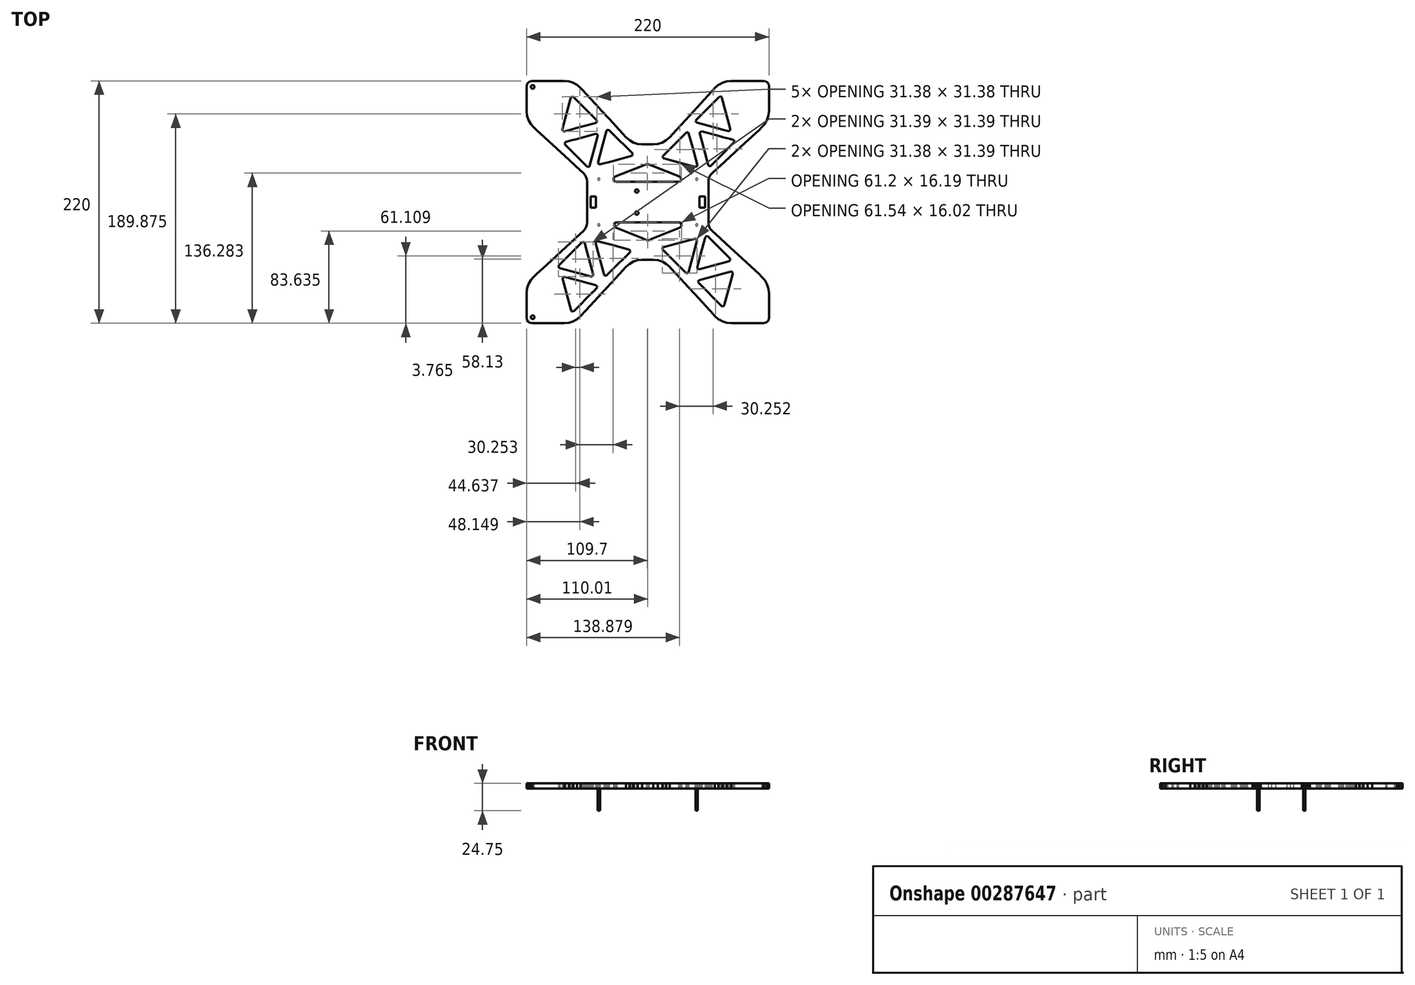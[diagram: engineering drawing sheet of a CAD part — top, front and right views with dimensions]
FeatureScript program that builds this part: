
annotation { "Feature Type Name" : "Feature", "Feature Type Description" : "" }
export const myFeature = defineFeature(function(context is Context, id is Id, definition is map)
    precondition{}
    {
        {
            var Q0;
            Q0=qCreatedBy(makeId("Top.planeOp"),FACE);
            var sketch = newSketch(context, id + "F0", { "sketchPlane" : qUnion([Q0])});
            skLineSegment(sketch, "E0", {"start": v(110, -105) * mm, "end": v(109.97, -105.11) * mm});
            skLineSegment(sketch, "E1", {"start": v(109.97, -105.11) * mm, "end": v(109.33, -107.5) * mm});
            skLineSegment(sketch, "E2", {"start": v(109.33, -107.5) * mm, "end": v(107.5, -109.33) * mm});
            skLineSegment(sketch, "E3", {"start": v(107.5, -109.33) * mm, "end": v(105.11, -109.97) * mm});
            skLineSegment(sketch, "E4", {"start": v(105.11, -109.97) * mm, "end": v(105, -110) * mm});
            skLineSegment(sketch, "E5", {"start": v(105, -110) * mm, "end": v(75.71, -110) * mm});
            skLineSegment(sketch, "E6", {"start": v(75.71, -110) * mm, "end": v(71.6, -109.58) * mm});
            skLineSegment(sketch, "E7", {"start": v(71.6, -109.58) * mm, "end": v(67.68, -108.32) * mm});
            skLineSegment(sketch, "E8", {"start": v(67.68, -108.32) * mm, "end": v(65.54, -107.1) * mm});
            skLineSegment(sketch, "E9", {"start": v(65.54, -107.1) * mm, "end": v(64.1, -106.29) * mm});
            skLineSegment(sketch, "E10", {"start": v(64.1, -106.29) * mm, "end": v(61, -103.56) * mm});
            skLineSegment(sketch, "E11", {"start": v(61, -103.56) * mm, "end": v(60.02, -102.49) * mm});
            skLineSegment(sketch, "E12", {"start": v(60.02, -102.49) * mm, "end": v(59.43, -101.85) * mm});
            skLineSegment(sketch, "E13", {"start": v(59.43, -101.85) * mm, "end": v(42.66, -83.66) * mm});
            skLineSegment(sketch, "E14", {"start": v(42.66, -83.66) * mm, "end": v(37.1, -77.62) * mm});
            skLineSegment(sketch, "E15", {"start": v(37.1, -77.62) * mm, "end": v(25.96, -65.54) * mm});
            skLineSegment(sketch, "E16", {"start": v(25.96, -65.54) * mm, "end": v(20.43, -59.54) * mm});
            skLineSegment(sketch, "E17", {"start": v(20.43, -59.54) * mm, "end": v(19.77, -58.82) * mm});
            skLineSegment(sketch, "E18", {"start": v(19.77, -58.82) * mm, "end": v(16.67, -56.1) * mm});
            skLineSegment(sketch, "E19", {"start": v(16.67, -56.1) * mm, "end": v(13.09, -54.06) * mm});
            skLineSegment(sketch, "E20", {"start": v(13.09, -54.06) * mm, "end": v(9.16, -52.8) * mm});
            skLineSegment(sketch, "E21", {"start": v(9.16, -52.8) * mm, "end": v(5.06, -52.37) * mm});
            skLineSegment(sketch, "E22", {"start": v(5.06, -52.37) * mm, "end": v(-5.06, -52.37) * mm});
            skLineSegment(sketch, "E23", {"start": v(-5.06, -52.37) * mm, "end": v(-9.16, -52.8) * mm});
            skLineSegment(sketch, "E24", {"start": v(-9.16, -52.8) * mm, "end": v(-13.1, -54.06) * mm});
            skLineSegment(sketch, "E25", {"start": v(-13.1, -54.06) * mm, "end": v(-16.67, -56.1) * mm});
            skLineSegment(sketch, "E26", {"start": v(-16.67, -56.1) * mm, "end": v(-19.77, -58.82) * mm});
            skLineSegment(sketch, "E27", {"start": v(-19.77, -58.82) * mm, "end": v(-25.96, -65.54) * mm});
            skLineSegment(sketch, "E28", {"start": v(-25.96, -65.54) * mm, "end": v(-32.77, -72.92) * mm});
            skLineSegment(sketch, "E29", {"start": v(-32.77, -72.92) * mm, "end": v(-37.77, -78.35) * mm});
            skLineSegment(sketch, "E30", {"start": v(-37.77, -78.35) * mm, "end": v(-38.62, -79.27) * mm});
            skLineSegment(sketch, "E31", {"start": v(-38.62, -79.27) * mm, "end": v(-39.42, -80.14) * mm});
            skLineSegment(sketch, "E32", {"start": v(-39.42, -80.14) * mm, "end": v(-41.06, -81.92) * mm});
            skLineSegment(sketch, "E33", {"start": v(-41.06, -81.92) * mm, "end": v(-56.16, -98.3) * mm});
            skLineSegment(sketch, "E34", {"start": v(-56.16, -98.3) * mm, "end": v(-61, -103.56) * mm});
            skLineSegment(sketch, "E35", {"start": v(-61, -103.56) * mm, "end": v(-64.1, -106.29) * mm});
            skLineSegment(sketch, "E36", {"start": v(-64.1, -106.29) * mm, "end": v(-65.54, -107.1) * mm});
            skLineSegment(sketch, "E37", {"start": v(-65.54, -107.1) * mm, "end": v(-67.68, -108.32) * mm});
            skLineSegment(sketch, "E38", {"start": v(-67.68, -108.32) * mm, "end": v(-71.6, -109.58) * mm});
            skLineSegment(sketch, "E39", {"start": v(-71.6, -109.58) * mm, "end": v(-75.71, -110) * mm});
            skLineSegment(sketch, "E40", {"start": v(-75.71, -110) * mm, "end": v(-105, -110) * mm});
            skLineSegment(sketch, "E41", {"start": v(-105, -110) * mm, "end": v(-106.91, -109.62) * mm});
            skLineSegment(sketch, "E42", {"start": v(-106.91, -109.62) * mm, "end": v(-108.53, -108.54) * mm});
            skLineSegment(sketch, "E43", {"start": v(-108.53, -108.54) * mm, "end": v(-109.62, -106.92) * mm});
            skLineSegment(sketch, "E44", {"start": v(-109.62, -106.92) * mm, "end": v(-110, -105) * mm});
            skLineSegment(sketch, "E45", {"start": v(-110, -105) * mm, "end": v(-110, -82.51) * mm});
            skLineSegment(sketch, "E46", {"start": v(-110, -82.51) * mm, "end": v(-109.58, -78.41) * mm});
            skLineSegment(sketch, "E47", {"start": v(-109.58, -78.41) * mm, "end": v(-108.32, -74.48) * mm});
            skLineSegment(sketch, "E48", {"start": v(-108.32, -74.48) * mm, "end": v(-106.28, -70.9) * mm});
            skLineSegment(sketch, "E49", {"start": v(-106.28, -70.9) * mm, "end": v(-103.55, -67.8) * mm});
            skLineSegment(sketch, "E50", {"start": v(-103.55, -67.8) * mm, "end": v(-101.1, -65.54) * mm});
            skLineSegment(sketch, "E51", {"start": v(-101.1, -65.54) * mm, "end": v(-91.63, -56.8) * mm});
            skLineSegment(sketch, "E52", {"start": v(-91.63, -56.8) * mm, "end": v(-65.54, -32.76) * mm});
            skLineSegment(sketch, "E53", {"start": v(-65.54, -32.76) * mm, "end": v(-58.22, -26.01) * mm});
            skLineSegment(sketch, "E54", {"start": v(-58.22, -26.01) * mm, "end": v(-56.86, -24.47) * mm});
            skLineSegment(sketch, "E55", {"start": v(-56.86, -24.47) * mm, "end": v(-55.84, -22.68) * mm});
            skLineSegment(sketch, "E56", {"start": v(-55.84, -22.68) * mm, "end": v(-55.21, -20.71) * mm});
            skLineSegment(sketch, "E57", {"start": v(-55.21, -20.71) * mm, "end": v(-55, -18.66) * mm});
            skLineSegment(sketch, "E58", {"start": v(-55, -18.66) * mm, "end": v(-55, 18.67) * mm});
            skLineSegment(sketch, "E59", {"start": v(-55, 18.67) * mm, "end": v(-55.21, 20.72) * mm});
            skLineSegment(sketch, "E60", {"start": v(-55.21, 20.72) * mm, "end": v(-55.84, 22.68) * mm});
            skLineSegment(sketch, "E61", {"start": v(-55.84, 22.68) * mm, "end": v(-56.86, 24.47) * mm});
            skLineSegment(sketch, "E62", {"start": v(-56.86, 24.47) * mm, "end": v(-58.22, 26.02) * mm});
            skLineSegment(sketch, "E63", {"start": v(-58.22, 26.02) * mm, "end": v(-65.54, 32.76) * mm});
            skLineSegment(sketch, "E64", {"start": v(-65.54, 32.76) * mm, "end": v(-66.26, 33.43) * mm});
            skLineSegment(sketch, "E65", {"start": v(-66.26, 33.43) * mm, "end": v(-75.44, 41.9) * mm});
            skLineSegment(sketch, "E66", {"start": v(-75.44, 41.9) * mm, "end": v(-101.1, 65.54) * mm});
            skLineSegment(sketch, "E67", {"start": v(-101.1, 65.54) * mm, "end": v(-103.55, 67.8) * mm});
            skLineSegment(sketch, "E68", {"start": v(-103.55, 67.8) * mm, "end": v(-106.28, 70.9) * mm});
            skLineSegment(sketch, "E69", {"start": v(-106.28, 70.9) * mm, "end": v(-108.32, 74.48) * mm});
            skLineSegment(sketch, "E70", {"start": v(-108.32, 74.48) * mm, "end": v(-109.58, 78.41) * mm});
            skLineSegment(sketch, "E71", {"start": v(-109.58, 78.41) * mm, "end": v(-110, 82.51) * mm});
            skLineSegment(sketch, "E72", {"start": v(-110, 82.51) * mm, "end": v(-110, 105) * mm});
            skLineSegment(sketch, "E73", {"start": v(-110, 105) * mm, "end": v(-109.97, 105.12) * mm});
            skLineSegment(sketch, "E74", {"start": v(-109.97, 105.12) * mm, "end": v(-109.33, 107.5) * mm});
            skLineSegment(sketch, "E75", {"start": v(-109.33, 107.5) * mm, "end": v(-108.87, 107.96) * mm});
            skLineSegment(sketch, "E76", {"start": v(-108.87, 107.96) * mm, "end": v(-107.5, 109.33) * mm});
            skLineSegment(sketch, "E77", {"start": v(-107.5, 109.33) * mm, "end": v(-105.11, 109.97) * mm});
            skLineSegment(sketch, "E78", {"start": v(-105.11, 109.97) * mm, "end": v(-105, 110) * mm});
            skLineSegment(sketch, "E79", {"start": v(-105, 110) * mm, "end": v(-75.71, 110) * mm});
            skLineSegment(sketch, "E80", {"start": v(-75.71, 110) * mm, "end": v(-71.6, 109.58) * mm});
            skLineSegment(sketch, "E81", {"start": v(-71.6, 109.58) * mm, "end": v(-67.68, 108.32) * mm});
            skLineSegment(sketch, "E82", {"start": v(-67.68, 108.32) * mm, "end": v(-65.54, 107.1) * mm});
            skLineSegment(sketch, "E83", {"start": v(-65.54, 107.1) * mm, "end": v(-64.1, 106.29) * mm});
            skLineSegment(sketch, "E84", {"start": v(-64.1, 106.29) * mm, "end": v(-61, 103.56) * mm});
            skLineSegment(sketch, "E85", {"start": v(-61, 103.56) * mm, "end": v(-59.4, 101.81) * mm});
            skLineSegment(sketch, "E86", {"start": v(-59.4, 101.81) * mm, "end": v(-43.95, 85.06) * mm});
            skLineSegment(sketch, "E87", {"start": v(-43.95, 85.06) * mm, "end": v(-42.3, 83.27) * mm});
            skLineSegment(sketch, "E88", {"start": v(-42.3, 83.27) * mm, "end": v(-34.8, 75.14) * mm});
            skLineSegment(sketch, "E89", {"start": v(-34.8, 75.14) * mm, "end": v(-25.96, 65.54) * mm});
            skLineSegment(sketch, "E90", {"start": v(-25.96, 65.54) * mm, "end": v(-19.77, 58.82) * mm});
            skLineSegment(sketch, "E91", {"start": v(-19.77, 58.82) * mm, "end": v(-16.67, 56.1) * mm});
            skLineSegment(sketch, "E92", {"start": v(-16.67, 56.1) * mm, "end": v(-13.1, 54.06) * mm});
            skLineSegment(sketch, "E93", {"start": v(-13.1, 54.06) * mm, "end": v(-9.16, 52.8) * mm});
            skLineSegment(sketch, "E94", {"start": v(-9.16, 52.8) * mm, "end": v(-5.06, 52.38) * mm});
            skLineSegment(sketch, "E95", {"start": v(-5.06, 52.38) * mm, "end": v(5.06, 52.38) * mm});
            skLineSegment(sketch, "E96", {"start": v(5.06, 52.38) * mm, "end": v(9.16, 52.8) * mm});
            skLineSegment(sketch, "E97", {"start": v(9.16, 52.8) * mm, "end": v(13.09, 54.06) * mm});
            skLineSegment(sketch, "E98", {"start": v(13.09, 54.06) * mm, "end": v(16.67, 56.1) * mm});
            skLineSegment(sketch, "E99", {"start": v(16.67, 56.1) * mm, "end": v(19.77, 58.82) * mm});
            skLineSegment(sketch, "E100", {"start": v(19.77, 58.82) * mm, "end": v(25.96, 65.54) * mm});
            skLineSegment(sketch, "E101", {"start": v(25.96, 65.54) * mm, "end": v(34.46, 74.76) * mm});
            skLineSegment(sketch, "E102", {"start": v(34.46, 74.76) * mm, "end": v(45, 86.2) * mm});
            skLineSegment(sketch, "E103", {"start": v(45, 86.2) * mm, "end": v(61, 103.56) * mm});
            skLineSegment(sketch, "E104", {"start": v(61, 103.56) * mm, "end": v(64.1, 106.29) * mm});
            skLineSegment(sketch, "E105", {"start": v(64.1, 106.29) * mm, "end": v(65.54, 107.1) * mm});
            skLineSegment(sketch, "E106", {"start": v(65.54, 107.1) * mm, "end": v(67.68, 108.32) * mm});
            skLineSegment(sketch, "E107", {"start": v(67.68, 108.32) * mm, "end": v(71.6, 109.58) * mm});
            skLineSegment(sketch, "E108", {"start": v(71.6, 109.58) * mm, "end": v(75.71, 110) * mm});
            skLineSegment(sketch, "E109", {"start": v(75.71, 110) * mm, "end": v(105, 110) * mm});
            skLineSegment(sketch, "E110", {"start": v(105, 110) * mm, "end": v(106.91, 109.62) * mm});
            skLineSegment(sketch, "E111", {"start": v(106.91, 109.62) * mm, "end": v(107.98, 108.9) * mm});
            skLineSegment(sketch, "E112", {"start": v(107.98, 108.9) * mm, "end": v(108.53, 108.54) * mm});
            skLineSegment(sketch, "E113", {"start": v(108.53, 108.54) * mm, "end": v(109.62, 106.92) * mm});
            skLineSegment(sketch, "E114", {"start": v(109.62, 106.92) * mm, "end": v(109.98, 105.13) * mm});
            skLineSegment(sketch, "E115", {"start": v(109.98, 105.13) * mm, "end": v(110, 105) * mm});
            skLineSegment(sketch, "E116", {"start": v(110, 105) * mm, "end": v(110, 82.51) * mm});
            skLineSegment(sketch, "E117", {"start": v(110, 82.51) * mm, "end": v(109.58, 78.41) * mm});
            skLineSegment(sketch, "E118", {"start": v(109.58, 78.41) * mm, "end": v(108.32, 74.48) * mm});
            skLineSegment(sketch, "E119", {"start": v(108.32, 74.48) * mm, "end": v(106.28, 70.9) * mm});
            skLineSegment(sketch, "E120", {"start": v(106.28, 70.9) * mm, "end": v(103.56, 67.8) * mm});
            skLineSegment(sketch, "E121", {"start": v(103.56, 67.8) * mm, "end": v(101.1, 65.54) * mm});
            skLineSegment(sketch, "E122", {"start": v(101.1, 65.54) * mm, "end": v(88.12, 53.58) * mm});
            skLineSegment(sketch, "E123", {"start": v(88.12, 53.58) * mm, "end": v(65.54, 32.76) * mm});
            skLineSegment(sketch, "E124", {"start": v(65.54, 32.76) * mm, "end": v(63.4, 30.8) * mm});
            skLineSegment(sketch, "E125", {"start": v(63.4, 30.8) * mm, "end": v(58.22, 26.02) * mm});
            skLineSegment(sketch, "E126", {"start": v(58.22, 26.02) * mm, "end": v(56.86, 24.47) * mm});
            skLineSegment(sketch, "E127", {"start": v(56.86, 24.47) * mm, "end": v(55.84, 22.68) * mm});
            skLineSegment(sketch, "E128", {"start": v(55.84, 22.68) * mm, "end": v(55.21, 20.72) * mm});
            skLineSegment(sketch, "E129", {"start": v(55.21, 20.72) * mm, "end": v(55, 18.67) * mm});
            skLineSegment(sketch, "E130", {"start": v(55, 18.67) * mm, "end": v(55, -18.66) * mm});
            skLineSegment(sketch, "E131", {"start": v(55, -18.66) * mm, "end": v(55.21, -20.71) * mm});
            skLineSegment(sketch, "E132", {"start": v(55.21, -20.71) * mm, "end": v(55.84, -22.68) * mm});
            skLineSegment(sketch, "E133", {"start": v(55.84, -22.68) * mm, "end": v(56.86, -24.47) * mm});
            skLineSegment(sketch, "E134", {"start": v(56.86, -24.47) * mm, "end": v(58.22, -26.01) * mm});
            skLineSegment(sketch, "E135", {"start": v(58.22, -26.01) * mm, "end": v(65.54, -32.76) * mm});
            skLineSegment(sketch, "E136", {"start": v(65.54, -32.76) * mm, "end": v(66.29, -33.45) * mm});
            skLineSegment(sketch, "E137", {"start": v(66.29, -33.45) * mm, "end": v(75, -41.48) * mm});
            skLineSegment(sketch, "E138", {"start": v(75, -41.48) * mm, "end": v(81.72, -47.68) * mm});
            skLineSegment(sketch, "E139", {"start": v(81.72, -47.68) * mm, "end": v(101.1, -65.54) * mm});
            skLineSegment(sketch, "E140", {"start": v(101.1, -65.54) * mm, "end": v(103.56, -67.8) * mm});
            skLineSegment(sketch, "E141", {"start": v(103.56, -67.8) * mm, "end": v(106.28, -70.9) * mm});
            skLineSegment(sketch, "E142", {"start": v(106.28, -70.9) * mm, "end": v(108.32, -74.48) * mm});
            skLineSegment(sketch, "E143", {"start": v(108.32, -74.48) * mm, "end": v(109.58, -78.41) * mm});
            skLineSegment(sketch, "E144", {"start": v(109.58, -78.41) * mm, "end": v(110, -82.51) * mm});
            skLineSegment(sketch, "E145", {"start": v(110, -82.51) * mm, "end": v(110, -105) * mm});
            skLineSegment(sketch, "E146", {"start": v(-43.2, 34.18) * mm, "end": v(-32.77, 36.98) * mm});
            skLineSegment(sketch, "E147", {"start": v(-32.77, 36.98) * mm, "end": v(-14.76, 41.8) * mm});
            skLineSegment(sketch, "E148", {"start": v(-14.76, 41.8) * mm, "end": v(-13.92, 42.4) * mm});
            skLineSegment(sketch, "E149", {"start": v(-13.92, 42.4) * mm, "end": v(-13.66, 43.38) * mm});
            skLineSegment(sketch, "E150", {"start": v(-13.66, 43.38) * mm, "end": v(-14.1, 44.31) * mm});
            skLineSegment(sketch, "E151", {"start": v(-14.1, 44.31) * mm, "end": v(-32.77, 62.99) * mm});
            skLineSegment(sketch, "E152", {"start": v(-32.77, 62.99) * mm, "end": v(-34.9, 65.12) * mm});
            skLineSegment(sketch, "E153", {"start": v(-34.9, 65.12) * mm, "end": v(-34.91, 65.13) * mm});
            skLineSegment(sketch, "E154", {"start": v(-34.91, 65.13) * mm, "end": v(-35.78, 65.54) * mm});
            skLineSegment(sketch, "E155", {"start": v(-35.78, 65.54) * mm, "end": v(-35.84, 65.57) * mm});
            skLineSegment(sketch, "E156", {"start": v(-35.84, 65.57) * mm, "end": v(-35.95, 65.54) * mm});
            skLineSegment(sketch, "E157", {"start": v(-35.95, 65.54) * mm, "end": v(-36.83, 65.3) * mm});
            skLineSegment(sketch, "E158", {"start": v(-36.83, 65.3) * mm, "end": v(-37.42, 64.46) * mm});
            skLineSegment(sketch, "E159", {"start": v(-37.42, 64.46) * mm, "end": v(-37.43, 64.44) * mm});
            skLineSegment(sketch, "E160", {"start": v(-37.43, 64.44) * mm, "end": v(-41.52, 49.15) * mm});
            skLineSegment(sketch, "E161", {"start": v(-41.52, 49.15) * mm, "end": v(-45.04, 36.02) * mm});
            skLineSegment(sketch, "E162", {"start": v(-45.04, 36.02) * mm, "end": v(-44.95, 35) * mm});
            skLineSegment(sketch, "E163", {"start": v(-44.95, 35) * mm, "end": v(-44.23, 34.27) * mm});
            skLineSegment(sketch, "E164", {"start": v(-44.23, 34.27) * mm, "end": v(-43.2, 34.18) * mm});
            skLineSegment(sketch, "E165", {"start": v(-58.87, -36.18) * mm, "end": v(-59.8, -36.61) * mm});
            skLineSegment(sketch, "E166", {"start": v(-59.8, -36.61) * mm, "end": v(-65.54, -42.35) * mm});
            skLineSegment(sketch, "E167", {"start": v(-65.54, -42.35) * mm, "end": v(-80.62, -57.43) * mm});
            skLineSegment(sketch, "E168", {"start": v(-80.62, -57.43) * mm, "end": v(-81.06, -58.36) * mm});
            skLineSegment(sketch, "E169", {"start": v(-81.06, -58.36) * mm, "end": v(-80.79, -59.35) * mm});
            skLineSegment(sketch, "E170", {"start": v(-80.79, -59.35) * mm, "end": v(-79.95, -59.94) * mm});
            skLineSegment(sketch, "E171", {"start": v(-79.95, -59.94) * mm, "end": v(-65.54, -63.8) * mm});
            skLineSegment(sketch, "E172", {"start": v(-65.54, -63.8) * mm, "end": v(-59.07, -65.54) * mm});
            skLineSegment(sketch, "E173", {"start": v(-59.07, -65.54) * mm, "end": v(-51.5, -67.56) * mm});
            skLineSegment(sketch, "E174", {"start": v(-51.5, -67.56) * mm, "end": v(-50.49, -67.47) * mm});
            skLineSegment(sketch, "E175", {"start": v(-50.49, -67.47) * mm, "end": v(-49.76, -66.75) * mm});
            skLineSegment(sketch, "E176", {"start": v(-49.76, -66.75) * mm, "end": v(-49.67, -65.73) * mm});
            skLineSegment(sketch, "E177", {"start": v(-49.67, -65.73) * mm, "end": v(-49.72, -65.54) * mm});
            skLineSegment(sketch, "E178", {"start": v(-49.72, -65.54) * mm, "end": v(-49.74, -65.46) * mm});
            skLineSegment(sketch, "E179", {"start": v(-49.74, -65.46) * mm, "end": v(-55.38, -44.43) * mm});
            skLineSegment(sketch, "E180", {"start": v(-55.38, -44.43) * mm, "end": v(-57.3, -37.28) * mm});
            skLineSegment(sketch, "E181", {"start": v(-57.3, -37.28) * mm, "end": v(-57.81, -36.53) * mm});
            skLineSegment(sketch, "E182", {"start": v(-57.81, -36.53) * mm, "end": v(-57.88, -36.44) * mm});
            skLineSegment(sketch, "E183", {"start": v(-57.88, -36.44) * mm, "end": v(-58.87, -36.18) * mm});
            skLineSegment(sketch, "E184", {"start": v(65.54, 66.43) * mm, "end": v(68.87, 65.54) * mm});
            skLineSegment(sketch, "E185", {"start": v(68.87, 65.54) * mm, "end": v(72.99, 64.43) * mm});
            skLineSegment(sketch, "E186", {"start": v(72.99, 64.43) * mm, "end": v(74, 64.52) * mm});
            skLineSegment(sketch, "E187", {"start": v(74, 64.52) * mm, "end": v(74.73, 65.25) * mm});
            skLineSegment(sketch, "E188", {"start": v(74.73, 65.25) * mm, "end": v(74.76, 65.54) * mm});
            skLineSegment(sketch, "E189", {"start": v(74.76, 65.54) * mm, "end": v(74.82, 66.27) * mm});
            skLineSegment(sketch, "E190", {"start": v(74.82, 66.27) * mm, "end": v(67.2, 94.71) * mm});
            skLineSegment(sketch, "E191", {"start": v(67.2, 94.71) * mm, "end": v(66.62, 95.55) * mm});
            skLineSegment(sketch, "E192", {"start": v(66.62, 95.55) * mm, "end": v(65.62, 95.82) * mm});
            skLineSegment(sketch, "E193", {"start": v(65.62, 95.82) * mm, "end": v(65.54, 95.78) * mm});
            skLineSegment(sketch, "E194", {"start": v(65.54, 95.78) * mm, "end": v(64.7, 95.39) * mm});
            skLineSegment(sketch, "E195", {"start": v(64.7, 95.39) * mm, "end": v(43.87, 74.57) * mm});
            skLineSegment(sketch, "E196", {"start": v(43.87, 74.57) * mm, "end": v(43.44, 73.64) * mm});
            skLineSegment(sketch, "E197", {"start": v(43.44, 73.64) * mm, "end": v(43.7, 72.65) * mm});
            skLineSegment(sketch, "E198", {"start": v(43.7, 72.65) * mm, "end": v(44.55, 72.06) * mm});
            skLineSegment(sketch, "E199", {"start": v(44.55, 72.06) * mm, "end": v(65.54, 66.43) * mm});
            skLineSegment(sketch, "E200", {"start": v(-17.01, -43.07) * mm, "end": v(-32.77, -38.85) * mm});
            skLineSegment(sketch, "E201", {"start": v(-32.77, -38.85) * mm, "end": v(-45.45, -35.45) * mm});
            skLineSegment(sketch, "E202", {"start": v(-45.45, -35.45) * mm, "end": v(-46.48, -35.54) * mm});
            skLineSegment(sketch, "E203", {"start": v(-46.48, -35.54) * mm, "end": v(-47.2, -36.26) * mm});
            skLineSegment(sketch, "E204", {"start": v(-47.2, -36.26) * mm, "end": v(-47.3, -37.28) * mm});
            skLineSegment(sketch, "E205", {"start": v(-47.3, -37.28) * mm, "end": v(-39.72, -65.54) * mm});
            skLineSegment(sketch, "E206", {"start": v(-39.72, -65.54) * mm, "end": v(-39.67, -65.73) * mm});
            skLineSegment(sketch, "E207", {"start": v(-39.67, -65.73) * mm, "end": v(-39.08, -66.57) * mm});
            skLineSegment(sketch, "E208", {"start": v(-39.08, -66.57) * mm, "end": v(-38.1, -66.83) * mm});
            skLineSegment(sketch, "E209", {"start": v(-38.1, -66.83) * mm, "end": v(-37.16, -66.4) * mm});
            skLineSegment(sketch, "E210", {"start": v(-37.16, -66.4) * mm, "end": v(-36.3, -65.54) * mm});
            skLineSegment(sketch, "E211", {"start": v(-36.3, -65.54) * mm, "end": v(-32.77, -62) * mm});
            skLineSegment(sketch, "E212", {"start": v(-32.77, -62) * mm, "end": v(-16.34, -45.58) * mm});
            skLineSegment(sketch, "E213", {"start": v(-16.34, -45.58) * mm, "end": v(-15.9, -44.65) * mm});
            skLineSegment(sketch, "E214", {"start": v(-15.9, -44.65) * mm, "end": v(-16.17, -43.65) * mm});
            skLineSegment(sketch, "E215", {"start": v(-16.17, -43.65) * mm, "end": v(-17.01, -43.07) * mm});
            skLineSegment(sketch, "E216", {"start": v(78.32, 55.84) * mm, "end": v(77.48, 56.43) * mm});
            skLineSegment(sketch, "E217", {"start": v(77.48, 56.43) * mm, "end": v(74.05, 57.35) * mm});
            skLineSegment(sketch, "E218", {"start": v(74.05, 57.35) * mm, "end": v(68.35, 58.88) * mm});
            skLineSegment(sketch, "E219", {"start": v(68.35, 58.88) * mm, "end": v(65.54, 59.63) * mm});
            skLineSegment(sketch, "E220", {"start": v(65.54, 59.63) * mm, "end": v(49.04, 64.05) * mm});
            skLineSegment(sketch, "E221", {"start": v(49.04, 64.05) * mm, "end": v(48.02, 63.96) * mm});
            skLineSegment(sketch, "E222", {"start": v(48.02, 63.96) * mm, "end": v(47.3, 63.24) * mm});
            skLineSegment(sketch, "E223", {"start": v(47.3, 63.24) * mm, "end": v(47.2, 62.21) * mm});
            skLineSegment(sketch, "E224", {"start": v(47.2, 62.21) * mm, "end": v(50.7, 49.15) * mm});
            skLineSegment(sketch, "E225", {"start": v(50.7, 49.15) * mm, "end": v(54.82, 33.77) * mm});
            skLineSegment(sketch, "E226", {"start": v(54.82, 33.77) * mm, "end": v(55.41, 32.93) * mm});
            skLineSegment(sketch, "E227", {"start": v(55.41, 32.93) * mm, "end": v(56.02, 32.77) * mm});
            skLineSegment(sketch, "E228", {"start": v(56.02, 32.77) * mm, "end": v(56.4, 32.66) * mm});
            skLineSegment(sketch, "E229", {"start": v(56.4, 32.66) * mm, "end": v(56.62, 32.77) * mm});
            skLineSegment(sketch, "E230", {"start": v(56.62, 32.77) * mm, "end": v(57.33, 33.1) * mm});
            skLineSegment(sketch, "E231", {"start": v(57.33, 33.1) * mm, "end": v(65.54, 41.3) * mm});
            skLineSegment(sketch, "E232", {"start": v(65.54, 41.3) * mm, "end": v(78.16, 53.92) * mm});
            skLineSegment(sketch, "E233", {"start": v(78.16, 53.92) * mm, "end": v(78.59, 54.85) * mm});
            skLineSegment(sketch, "E234", {"start": v(78.59, 54.85) * mm, "end": v(78.32, 55.84) * mm});
            skLineSegment(sketch, "E235", {"start": v(-53.26, 32.1) * mm, "end": v(-52.79, 32.77) * mm});
            skLineSegment(sketch, "E236", {"start": v(-52.79, 32.77) * mm, "end": v(-52.67, 32.94) * mm});
            skLineSegment(sketch, "E237", {"start": v(-52.67, 32.94) * mm, "end": v(-48.33, 49.15) * mm});
            skLineSegment(sketch, "E238", {"start": v(-48.33, 49.15) * mm, "end": v(-45.43, 59.97) * mm});
            skLineSegment(sketch, "E239", {"start": v(-45.43, 59.97) * mm, "end": v(-45.52, 60.99) * mm});
            skLineSegment(sketch, "E240", {"start": v(-45.52, 60.99) * mm, "end": v(-46.24, 61.71) * mm});
            skLineSegment(sketch, "E241", {"start": v(-46.24, 61.71) * mm, "end": v(-47.26, 61.8) * mm});
            skLineSegment(sketch, "E242", {"start": v(-47.26, 61.8) * mm, "end": v(-65.54, 56.9) * mm});
            skLineSegment(sketch, "E243", {"start": v(-65.54, 56.9) * mm, "end": v(-68.56, 56.1) * mm});
            skLineSegment(sketch, "E244", {"start": v(-68.56, 56.1) * mm, "end": v(-74.3, 54.56) * mm});
            skLineSegment(sketch, "E245", {"start": v(-74.3, 54.56) * mm, "end": v(-75.13, 53.97) * mm});
            skLineSegment(sketch, "E246", {"start": v(-75.13, 53.97) * mm, "end": v(-75.4, 52.98) * mm});
            skLineSegment(sketch, "E247", {"start": v(-75.4, 52.98) * mm, "end": v(-74.96, 52.05) * mm});
            skLineSegment(sketch, "E248", {"start": v(-74.96, 52.05) * mm, "end": v(-65.54, 42.63) * mm});
            skLineSegment(sketch, "E249", {"start": v(-65.54, 42.63) * mm, "end": v(-55.68, 32.77) * mm});
            skLineSegment(sketch, "E250", {"start": v(-55.68, 32.77) * mm, "end": v(-55.18, 32.27) * mm});
            skLineSegment(sketch, "E251", {"start": v(-55.18, 32.27) * mm, "end": v(-54.25, 31.83) * mm});
            skLineSegment(sketch, "E252", {"start": v(-54.25, 31.83) * mm, "end": v(-53.26, 32.1) * mm});
            skLineSegment(sketch, "E253", {"start": v(-75.7, 64.18) * mm, "end": v(-70.65, 65.54) * mm});
            skLineSegment(sketch, "E254", {"start": v(-70.65, 65.54) * mm, "end": v(-65.54, 66.9) * mm});
            skLineSegment(sketch, "E255", {"start": v(-65.54, 66.9) * mm, "end": v(-48.52, 71.47) * mm});
            skLineSegment(sketch, "E256", {"start": v(-48.52, 71.47) * mm, "end": v(-47.26, 71.8) * mm});
            skLineSegment(sketch, "E257", {"start": v(-47.26, 71.8) * mm, "end": v(-46.42, 72.4) * mm});
            skLineSegment(sketch, "E258", {"start": v(-46.42, 72.4) * mm, "end": v(-46.16, 73.38) * mm});
            skLineSegment(sketch, "E259", {"start": v(-46.16, 73.38) * mm, "end": v(-46.6, 74.31) * mm});
            skLineSegment(sketch, "E260", {"start": v(-46.6, 74.31) * mm, "end": v(-67.41, 95.13) * mm});
            skLineSegment(sketch, "E261", {"start": v(-67.41, 95.13) * mm, "end": v(-68.34, 95.57) * mm});
            skLineSegment(sketch, "E262", {"start": v(-68.34, 95.57) * mm, "end": v(-69.33, 95.3) * mm});
            skLineSegment(sketch, "E263", {"start": v(-69.33, 95.3) * mm, "end": v(-69.92, 94.46) * mm});
            skLineSegment(sketch, "E264", {"start": v(-69.92, 94.46) * mm, "end": v(-77.54, 66.02) * mm});
            skLineSegment(sketch, "E265", {"start": v(-77.54, 66.02) * mm, "end": v(-77.5, 65.54) * mm});
            skLineSegment(sketch, "E266", {"start": v(-77.5, 65.54) * mm, "end": v(-77.45, 65) * mm});
            skLineSegment(sketch, "E267", {"start": v(-77.45, 65) * mm, "end": v(-76.73, 64.27) * mm});
            skLineSegment(sketch, "E268", {"start": v(-76.73, 64.27) * mm, "end": v(-75.7, 64.18) * mm});
            skLineSegment(sketch, "E269", {"start": v(30.35, -22.02) * mm, "end": v(30.61, -20.32) * mm});
            skLineSegment(sketch, "E270", {"start": v(30.61, -20.32) * mm, "end": v(29.73, -18.85) * mm});
            skLineSegment(sketch, "E271", {"start": v(29.73, -18.85) * mm, "end": v(28.12, -18.27) * mm});
            skLineSegment(sketch, "E272", {"start": v(28.12, -18.27) * mm, "end": v(-28.1, -18.27) * mm});
            skLineSegment(sketch, "E273", {"start": v(-28.1, -18.27) * mm, "end": v(-29.72, -18.85) * mm});
            skLineSegment(sketch, "E274", {"start": v(-29.72, -18.85) * mm, "end": v(-30.6, -20.33) * mm});
            skLineSegment(sketch, "E275", {"start": v(-30.6, -20.33) * mm, "end": v(-30.33, -22.02) * mm});
            skLineSegment(sketch, "E276", {"start": v(-30.33, -22.02) * mm, "end": v(-29.04, -23.16) * mm});
            skLineSegment(sketch, "E277", {"start": v(-29.04, -23.16) * mm, "end": v(-5.1, -32.77) * mm});
            skLineSegment(sketch, "E278", {"start": v(-5.1, -32.77) * mm, "end": v(-3.98, -33.22) * mm});
            skLineSegment(sketch, "E279", {"start": v(-3.98, -33.22) * mm, "end": v(-0.88, -34.46) * mm});
            skLineSegment(sketch, "E280", {"start": v(-0.88, -34.46) * mm, "end": v(0, -34.46) * mm});
            skLineSegment(sketch, "E281", {"start": v(0, -34.46) * mm, "end": v(1.01, -34.46) * mm});
            skLineSegment(sketch, "E282", {"start": v(1.01, -34.46) * mm, "end": v(3.68, -33.39) * mm});
            skLineSegment(sketch, "E283", {"start": v(3.68, -33.39) * mm, "end": v(5.22, -32.77) * mm});
            skLineSegment(sketch, "E284", {"start": v(5.22, -32.77) * mm, "end": v(29.07, -23.16) * mm});
            skLineSegment(sketch, "E285", {"start": v(29.07, -23.16) * mm, "end": v(30.35, -22.02) * mm});
            skLineSegment(sketch, "E286", {"start": v(-52, 5) * mm, "end": v(-52, -5) * mm});
            skLineSegment(sketch, "E287", {"start": v(-52, -5) * mm, "end": v(-47, -5) * mm});
            skLineSegment(sketch, "E288", {"start": v(-47, -5) * mm, "end": v(-47, 5) * mm});
            skLineSegment(sketch, "E289", {"start": v(-47, 5) * mm, "end": v(-52, 5) * mm});
            skLineSegment(sketch, "E290", {"start": v(75.23, -63.2) * mm, "end": v(66.52, -65.54) * mm});
            skLineSegment(sketch, "E291", {"start": v(66.52, -65.54) * mm, "end": v(65.54, -65.8) * mm});
            skLineSegment(sketch, "E292", {"start": v(65.54, -65.8) * mm, "end": v(46.8, -70.82) * mm});
            skLineSegment(sketch, "E293", {"start": v(46.8, -70.82) * mm, "end": v(45.95, -71.4) * mm});
            skLineSegment(sketch, "E294", {"start": v(45.95, -71.4) * mm, "end": v(45.69, -72.4) * mm});
            skLineSegment(sketch, "E295", {"start": v(45.69, -72.4) * mm, "end": v(46.12, -73.33) * mm});
            skLineSegment(sketch, "E296", {"start": v(46.12, -73.33) * mm, "end": v(66.94, -94.15) * mm});
            skLineSegment(sketch, "E297", {"start": v(66.94, -94.15) * mm, "end": v(67.87, -94.58) * mm});
            skLineSegment(sketch, "E298", {"start": v(67.87, -94.58) * mm, "end": v(68.86, -94.32) * mm});
            skLineSegment(sketch, "E299", {"start": v(68.86, -94.32) * mm, "end": v(69.45, -93.48) * mm});
            skLineSegment(sketch, "E300", {"start": v(69.45, -93.48) * mm, "end": v(76.94, -65.54) * mm});
            skLineSegment(sketch, "E301", {"start": v(76.94, -65.54) * mm, "end": v(77.07, -65.04) * mm});
            skLineSegment(sketch, "E302", {"start": v(77.07, -65.04) * mm, "end": v(76.98, -64.01) * mm});
            skLineSegment(sketch, "E303", {"start": v(76.98, -64.01) * mm, "end": v(76.26, -63.29) * mm});
            skLineSegment(sketch, "E304", {"start": v(76.26, -63.29) * mm, "end": v(75.23, -63.2) * mm});
            skLineSegment(sketch, "E305", {"start": v(-46.17, -76.16) * mm, "end": v(-46.61, -75.85) * mm});
            skLineSegment(sketch, "E306", {"start": v(-46.61, -75.85) * mm, "end": v(-47.01, -75.57) * mm});
            skLineSegment(sketch, "E307", {"start": v(-47.01, -75.57) * mm, "end": v(-49.15, -75) * mm});
            skLineSegment(sketch, "E308", {"start": v(-49.15, -75) * mm, "end": v(-65.54, -70.6) * mm});
            skLineSegment(sketch, "E309", {"start": v(-65.54, -70.6) * mm, "end": v(-75.45, -67.95) * mm});
            skLineSegment(sketch, "E310", {"start": v(-75.45, -67.95) * mm, "end": v(-76.48, -68.04) * mm});
            skLineSegment(sketch, "E311", {"start": v(-76.48, -68.04) * mm, "end": v(-77.2, -68.76) * mm});
            skLineSegment(sketch, "E312", {"start": v(-77.2, -68.76) * mm, "end": v(-77.3, -69.79) * mm});
            skLineSegment(sketch, "E313", {"start": v(-77.3, -69.79) * mm, "end": v(-69.67, -98.23) * mm});
            skLineSegment(sketch, "E314", {"start": v(-69.67, -98.23) * mm, "end": v(-69.61, -98.3) * mm});
            skLineSegment(sketch, "E315", {"start": v(-69.61, -98.3) * mm, "end": v(-69.08, -99.07) * mm});
            skLineSegment(sketch, "E316", {"start": v(-69.08, -99.07) * mm, "end": v(-68.1, -99.33) * mm});
            skLineSegment(sketch, "E317", {"start": v(-68.1, -99.33) * mm, "end": v(-67.16, -98.9) * mm});
            skLineSegment(sketch, "E318", {"start": v(-67.16, -98.9) * mm, "end": v(-66.56, -98.3) * mm});
            skLineSegment(sketch, "E319", {"start": v(-66.56, -98.3) * mm, "end": v(-50.18, -81.92) * mm});
            skLineSegment(sketch, "E320", {"start": v(-50.18, -81.92) * mm, "end": v(-49.15, -80.89) * mm});
            skLineSegment(sketch, "E321", {"start": v(-49.15, -80.89) * mm, "end": v(-46.34, -78.08) * mm});
            skLineSegment(sketch, "E322", {"start": v(-46.34, -78.08) * mm, "end": v(-45.9, -77.15) * mm});
            skLineSegment(sketch, "E323", {"start": v(-45.9, -77.15) * mm, "end": v(-46.17, -76.16) * mm});
            skLineSegment(sketch, "E324", {"start": v(74.66, -52.99) * mm, "end": v(74.92, -52) * mm});
            skLineSegment(sketch, "E325", {"start": v(74.92, -52) * mm, "end": v(74.5, -51.07) * mm});
            skLineSegment(sketch, "E326", {"start": v(74.5, -51.07) * mm, "end": v(57.52, -34.1) * mm});
            skLineSegment(sketch, "E327", {"start": v(57.52, -34.1) * mm, "end": v(56.2, -32.77) * mm});
            skLineSegment(sketch, "E328", {"start": v(56.2, -32.77) * mm, "end": v(55, -31.58) * mm});
            skLineSegment(sketch, "E329", {"start": v(55, -31.58) * mm, "end": v(54.7, -31.28) * mm});
            skLineSegment(sketch, "E330", {"start": v(54.7, -31.28) * mm, "end": v(53.78, -30.85) * mm});
            skLineSegment(sketch, "E331", {"start": v(53.78, -30.85) * mm, "end": v(52.79, -31.11) * mm});
            skLineSegment(sketch, "E332", {"start": v(52.79, -31.11) * mm, "end": v(52.2, -31.96) * mm});
            skLineSegment(sketch, "E333", {"start": v(52.2, -31.96) * mm, "end": v(51.98, -32.77) * mm});
            skLineSegment(sketch, "E334", {"start": v(51.98, -32.77) * mm, "end": v(47.97, -47.74) * mm});
            skLineSegment(sketch, "E335", {"start": v(47.97, -47.74) * mm, "end": v(44.95, -58.98) * mm});
            skLineSegment(sketch, "E336", {"start": v(44.95, -58.98) * mm, "end": v(45.05, -60) * mm});
            skLineSegment(sketch, "E337", {"start": v(45.05, -60) * mm, "end": v(45.77, -60.73) * mm});
            skLineSegment(sketch, "E338", {"start": v(45.77, -60.73) * mm, "end": v(46.8, -60.82) * mm});
            skLineSegment(sketch, "E339", {"start": v(46.8, -60.82) * mm, "end": v(65.54, -55.8) * mm});
            skLineSegment(sketch, "E340", {"start": v(65.54, -55.8) * mm, "end": v(68.08, -55.12) * mm});
            skLineSegment(sketch, "E341", {"start": v(68.08, -55.12) * mm, "end": v(73.82, -53.58) * mm});
            skLineSegment(sketch, "E342", {"start": v(73.82, -53.58) * mm, "end": v(74.66, -52.99) * mm});
            skLineSegment(sketch, "E343", {"start": v(-29.5, 23.18) * mm, "end": v(-30.8, 22.04) * mm});
            skLineSegment(sketch, "E344", {"start": v(-30.8, 22.04) * mm, "end": v(-31.07, 20.34) * mm});
            skLineSegment(sketch, "E345", {"start": v(-31.07, 20.34) * mm, "end": v(-30.2, 18.86) * mm});
            skLineSegment(sketch, "E346", {"start": v(-30.2, 18.86) * mm, "end": v(-28.58, 18.27) * mm});
            skLineSegment(sketch, "E347", {"start": v(-28.58, 18.27) * mm, "end": v(27.98, 18.27) * mm});
            skLineSegment(sketch, "E348", {"start": v(27.98, 18.27) * mm, "end": v(29.6, 18.86) * mm});
            skLineSegment(sketch, "E349", {"start": v(29.6, 18.86) * mm, "end": v(30.47, 20.34) * mm});
            skLineSegment(sketch, "E350", {"start": v(30.47, 20.34) * mm, "end": v(30.2, 22.04) * mm});
            skLineSegment(sketch, "E351", {"start": v(30.2, 22.04) * mm, "end": v(28.9, 23.18) * mm});
            skLineSegment(sketch, "E352", {"start": v(28.9, 23.18) * mm, "end": v(4.5, 32.77) * mm});
            skLineSegment(sketch, "E353", {"start": v(4.5, 32.77) * mm, "end": v(0.63, 34.3) * mm});
            skLineSegment(sketch, "E354", {"start": v(0.63, 34.3) * mm, "end": v(-1.23, 34.3) * mm});
            skLineSegment(sketch, "E355", {"start": v(-1.23, 34.3) * mm, "end": v(-5.1, 32.77) * mm});
            skLineSegment(sketch, "E356", {"start": v(-5.1, 32.77) * mm, "end": v(-29.5, 23.18) * mm});
            skLineSegment(sketch, "E357", {"start": v(52, -5) * mm, "end": v(52, 5) * mm});
            skLineSegment(sketch, "E358", {"start": v(52, 5) * mm, "end": v(47, 5) * mm});
            skLineSegment(sketch, "E359", {"start": v(47, 5) * mm, "end": v(47, -5) * mm});
            skLineSegment(sketch, "E360", {"start": v(47, -5) * mm, "end": v(52, -5) * mm});
            skLineSegment(sketch, "E361", {"start": v(14.55, 39.56) * mm, "end": v(32.77, 34.67) * mm});
            skLineSegment(sketch, "E362", {"start": v(32.77, 34.67) * mm, "end": v(39.87, 32.77) * mm});
            skLineSegment(sketch, "E363", {"start": v(39.87, 32.77) * mm, "end": v(42.99, 31.93) * mm});
            skLineSegment(sketch, "E364", {"start": v(42.99, 31.93) * mm, "end": v(44, 32.02) * mm});
            skLineSegment(sketch, "E365", {"start": v(44, 32.02) * mm, "end": v(44.73, 32.75) * mm});
            skLineSegment(sketch, "E366", {"start": v(44.73, 32.75) * mm, "end": v(44.74, 32.77) * mm});
            skLineSegment(sketch, "E367", {"start": v(44.74, 32.77) * mm, "end": v(44.82, 33.77) * mm});
            skLineSegment(sketch, "E368", {"start": v(44.82, 33.77) * mm, "end": v(40.7, 49.15) * mm});
            skLineSegment(sketch, "E369", {"start": v(40.7, 49.15) * mm, "end": v(37.2, 62.21) * mm});
            skLineSegment(sketch, "E370", {"start": v(37.2, 62.21) * mm, "end": v(36.62, 63.05) * mm});
            skLineSegment(sketch, "E371", {"start": v(36.62, 63.05) * mm, "end": v(35.62, 63.32) * mm});
            skLineSegment(sketch, "E372", {"start": v(35.62, 63.32) * mm, "end": v(34.7, 62.89) * mm});
            skLineSegment(sketch, "E373", {"start": v(34.7, 62.89) * mm, "end": v(13.87, 42.06) * mm});
            skLineSegment(sketch, "E374", {"start": v(13.87, 42.06) * mm, "end": v(13.44, 41.13) * mm});
            skLineSegment(sketch, "E375", {"start": v(13.44, 41.13) * mm, "end": v(13.7, 40.15) * mm});
            skLineSegment(sketch, "E376", {"start": v(13.7, 40.15) * mm, "end": v(14.55, 39.56) * mm});
            skLineSegment(sketch, "E377", {"start": v(13.19, -42.4) * mm, "end": v(13.62, -43.33) * mm});
            skLineSegment(sketch, "E378", {"start": v(13.62, -43.33) * mm, "end": v(34.44, -64.15) * mm});
            skLineSegment(sketch, "E379", {"start": v(34.44, -64.15) * mm, "end": v(35.37, -64.58) * mm});
            skLineSegment(sketch, "E380", {"start": v(35.37, -64.58) * mm, "end": v(36.36, -64.32) * mm});
            skLineSegment(sketch, "E381", {"start": v(36.36, -64.32) * mm, "end": v(36.95, -63.48) * mm});
            skLineSegment(sketch, "E382", {"start": v(36.95, -63.48) * mm, "end": v(44.57, -35.04) * mm});
            skLineSegment(sketch, "E383", {"start": v(44.57, -35.04) * mm, "end": v(44.48, -34.01) * mm});
            skLineSegment(sketch, "E384", {"start": v(44.48, -34.01) * mm, "end": v(43.76, -33.29) * mm});
            skLineSegment(sketch, "E385", {"start": v(43.76, -33.29) * mm, "end": v(42.74, -33.2) * mm});
            skLineSegment(sketch, "E386", {"start": v(42.74, -33.2) * mm, "end": v(32.77, -35.87) * mm});
            skLineSegment(sketch, "E387", {"start": v(32.77, -35.87) * mm, "end": v(14.3, -40.82) * mm});
            skLineSegment(sketch, "E388", {"start": v(14.3, -40.82) * mm, "end": v(13.45, -41.4) * mm});
            skLineSegment(sketch, "E389", {"start": v(13.45, -41.4) * mm, "end": v(13.19, -42.4) * mm});
            skSolve(sketch);
        }
        {
            var Q0;
            Q0=qSketchRegion(id+"F0",true);
            extrude(context, id + "F1", {"entities" : qUnion([Q0]), "depth" : 4.75 * mm, "offsetDistance" : 25 * mm});
        }
        {
            var Q0;
            Q0=makeQuery(id+"F1.opExtrude","CAP_FACE",FACE,{"disambiguationData":[OSD([sQuery(id+"F0.wireOp",EDGE,"E0"),sQuery(id+"F0.wireOp",EDGE,"E1"),sQuery(id+"F0.wireOp",EDGE,"E2"),sQuery(id+"F0.wireOp",EDGE,"E3"),sQuery(id+"F0.wireOp",EDGE,"E4"),sQuery(id+"F0.wireOp",EDGE,"E5"),sQuery(id+"F0.wireOp",EDGE,"E6"),sQuery(id+"F0.wireOp",EDGE,"E7"),sQuery(id+"F0.wireOp",EDGE,"E8"),sQuery(id+"F0.wireOp",EDGE,"E9"),sQuery(id+"F0.wireOp",EDGE,"E10"),sQuery(id+"F0.wireOp",EDGE,"E11"),sQuery(id+"F0.wireOp",EDGE,"E12"),sQuery(id+"F0.wireOp",EDGE,"E13"),sQuery(id+"F0.wireOp",EDGE,"E14"),sQuery(id+"F0.wireOp",EDGE,"E15"),sQuery(id+"F0.wireOp",EDGE,"E16"),sQuery(id+"F0.wireOp",EDGE,"E17"),sQuery(id+"F0.wireOp",EDGE,"E18"),sQuery(id+"F0.wireOp",EDGE,"E19"),sQuery(id+"F0.wireOp",EDGE,"E20"),sQuery(id+"F0.wireOp",EDGE,"E21"),sQuery(id+"F0.wireOp",EDGE,"E22"),sQuery(id+"F0.wireOp",EDGE,"E23"),sQuery(id+"F0.wireOp",EDGE,"E24"),sQuery(id+"F0.wireOp",EDGE,"E25"),sQuery(id+"F0.wireOp",EDGE,"E26"),sQuery(id+"F0.wireOp",EDGE,"E27"),sQuery(id+"F0.wireOp",EDGE,"E28"),sQuery(id+"F0.wireOp",EDGE,"E29"),sQuery(id+"F0.wireOp",EDGE,"E30"),sQuery(id+"F0.wireOp",EDGE,"E31"),sQuery(id+"F0.wireOp",EDGE,"E32"),sQuery(id+"F0.wireOp",EDGE,"E33"),sQuery(id+"F0.wireOp",EDGE,"E34"),sQuery(id+"F0.wireOp",EDGE,"E35"),sQuery(id+"F0.wireOp",EDGE,"E36"),sQuery(id+"F0.wireOp",EDGE,"E37"),sQuery(id+"F0.wireOp",EDGE,"E38"),sQuery(id+"F0.wireOp",EDGE,"E39"),sQuery(id+"F0.wireOp",EDGE,"E40"),sQuery(id+"F0.wireOp",EDGE,"E41"),sQuery(id+"F0.wireOp",EDGE,"E42"),sQuery(id+"F0.wireOp",EDGE,"E43"),sQuery(id+"F0.wireOp",EDGE,"E44"),sQuery(id+"F0.wireOp",EDGE,"E45"),sQuery(id+"F0.wireOp",EDGE,"E46"),sQuery(id+"F0.wireOp",EDGE,"E47"),sQuery(id+"F0.wireOp",EDGE,"E48"),sQuery(id+"F0.wireOp",EDGE,"E49"),sQuery(id+"F0.wireOp",EDGE,"E50"),sQuery(id+"F0.wireOp",EDGE,"E51"),sQuery(id+"F0.wireOp",EDGE,"E52"),sQuery(id+"F0.wireOp",EDGE,"E53"),sQuery(id+"F0.wireOp",EDGE,"E54"),sQuery(id+"F0.wireOp",EDGE,"E55"),sQuery(id+"F0.wireOp",EDGE,"E56"),sQuery(id+"F0.wireOp",EDGE,"E57"),sQuery(id+"F0.wireOp",EDGE,"E58"),sQuery(id+"F0.wireOp",EDGE,"E59"),sQuery(id+"F0.wireOp",EDGE,"E60"),sQuery(id+"F0.wireOp",EDGE,"E61"),sQuery(id+"F0.wireOp",EDGE,"E62"),sQuery(id+"F0.wireOp",EDGE,"E63"),sQuery(id+"F0.wireOp",EDGE,"E64"),sQuery(id+"F0.wireOp",EDGE,"E65"),sQuery(id+"F0.wireOp",EDGE,"E66"),sQuery(id+"F0.wireOp",EDGE,"E67"),sQuery(id+"F0.wireOp",EDGE,"E68"),sQuery(id+"F0.wireOp",EDGE,"E69"),sQuery(id+"F0.wireOp",EDGE,"E70"),sQuery(id+"F0.wireOp",EDGE,"E71"),sQuery(id+"F0.wireOp",EDGE,"E72"),sQuery(id+"F0.wireOp",EDGE,"E73"),sQuery(id+"F0.wireOp",EDGE,"E74"),sQuery(id+"F0.wireOp",EDGE,"E75"),sQuery(id+"F0.wireOp",EDGE,"E76"),sQuery(id+"F0.wireOp",EDGE,"E77"),sQuery(id+"F0.wireOp",EDGE,"E78"),sQuery(id+"F0.wireOp",EDGE,"E79"),sQuery(id+"F0.wireOp",EDGE,"E80"),sQuery(id+"F0.wireOp",EDGE,"E81"),sQuery(id+"F0.wireOp",EDGE,"E82"),sQuery(id+"F0.wireOp",EDGE,"E83"),sQuery(id+"F0.wireOp",EDGE,"E84"),sQuery(id+"F0.wireOp",EDGE,"E85"),sQuery(id+"F0.wireOp",EDGE,"E86"),sQuery(id+"F0.wireOp",EDGE,"E87"),sQuery(id+"F0.wireOp",EDGE,"E88"),sQuery(id+"F0.wireOp",EDGE,"E89"),sQuery(id+"F0.wireOp",EDGE,"E90"),sQuery(id+"F0.wireOp",EDGE,"E91"),sQuery(id+"F0.wireOp",EDGE,"E92"),sQuery(id+"F0.wireOp",EDGE,"E93"),sQuery(id+"F0.wireOp",EDGE,"E94"),sQuery(id+"F0.wireOp",EDGE,"E95"),sQuery(id+"F0.wireOp",EDGE,"E96"),sQuery(id+"F0.wireOp",EDGE,"E97"),sQuery(id+"F0.wireOp",EDGE,"E98"),sQuery(id+"F0.wireOp",EDGE,"E99"),sQuery(id+"F0.wireOp",EDGE,"E100"),sQuery(id+"F0.wireOp",EDGE,"E101"),sQuery(id+"F0.wireOp",EDGE,"E102"),sQuery(id+"F0.wireOp",EDGE,"E103"),sQuery(id+"F0.wireOp",EDGE,"E104"),sQuery(id+"F0.wireOp",EDGE,"E105"),sQuery(id+"F0.wireOp",EDGE,"E106"),sQuery(id+"F0.wireOp",EDGE,"E107"),sQuery(id+"F0.wireOp",EDGE,"E108"),sQuery(id+"F0.wireOp",EDGE,"E109"),sQuery(id+"F0.wireOp",EDGE,"E110"),sQuery(id+"F0.wireOp",EDGE,"E111"),sQuery(id+"F0.wireOp",EDGE,"E112"),sQuery(id+"F0.wireOp",EDGE,"E113"),sQuery(id+"F0.wireOp",EDGE,"E114"),sQuery(id+"F0.wireOp",EDGE,"E115"),sQuery(id+"F0.wireOp",EDGE,"E116"),sQuery(id+"F0.wireOp",EDGE,"E117"),sQuery(id+"F0.wireOp",EDGE,"E118"),sQuery(id+"F0.wireOp",EDGE,"E119"),sQuery(id+"F0.wireOp",EDGE,"E120"),sQuery(id+"F0.wireOp",EDGE,"E121"),sQuery(id+"F0.wireOp",EDGE,"E122"),sQuery(id+"F0.wireOp",EDGE,"E123"),sQuery(id+"F0.wireOp",EDGE,"E124"),sQuery(id+"F0.wireOp",EDGE,"E125"),sQuery(id+"F0.wireOp",EDGE,"E126"),sQuery(id+"F0.wireOp",EDGE,"E127"),sQuery(id+"F0.wireOp",EDGE,"E128"),sQuery(id+"F0.wireOp",EDGE,"E129"),sQuery(id+"F0.wireOp",EDGE,"E130"),sQuery(id+"F0.wireOp",EDGE,"E131"),sQuery(id+"F0.wireOp",EDGE,"E132"),sQuery(id+"F0.wireOp",EDGE,"E133"),sQuery(id+"F0.wireOp",EDGE,"E134"),sQuery(id+"F0.wireOp",EDGE,"E135"),sQuery(id+"F0.wireOp",EDGE,"E136"),sQuery(id+"F0.wireOp",EDGE,"E137"),sQuery(id+"F0.wireOp",EDGE,"E138"),sQuery(id+"F0.wireOp",EDGE,"E139"),sQuery(id+"F0.wireOp",EDGE,"E140"),sQuery(id+"F0.wireOp",EDGE,"E141"),sQuery(id+"F0.wireOp",EDGE,"E142"),sQuery(id+"F0.wireOp",EDGE,"E143"),sQuery(id+"F0.wireOp",EDGE,"E144"),sQuery(id+"F0.wireOp",EDGE,"E145"),sQuery(id+"F0.wireOp",EDGE,"E146"),sQuery(id+"F0.wireOp",EDGE,"E147"),sQuery(id+"F0.wireOp",EDGE,"E148"),sQuery(id+"F0.wireOp",EDGE,"E149"),sQuery(id+"F0.wireOp",EDGE,"E150"),sQuery(id+"F0.wireOp",EDGE,"E151"),sQuery(id+"F0.wireOp",EDGE,"E152"),sQuery(id+"F0.wireOp",EDGE,"E153"),sQuery(id+"F0.wireOp",EDGE,"E154"),sQuery(id+"F0.wireOp",EDGE,"E155"),sQuery(id+"F0.wireOp",EDGE,"E156"),sQuery(id+"F0.wireOp",EDGE,"E157"),sQuery(id+"F0.wireOp",EDGE,"E158"),sQuery(id+"F0.wireOp",EDGE,"E159"),sQuery(id+"F0.wireOp",EDGE,"E160"),sQuery(id+"F0.wireOp",EDGE,"E161"),sQuery(id+"F0.wireOp",EDGE,"E162"),sQuery(id+"F0.wireOp",EDGE,"E163"),sQuery(id+"F0.wireOp",EDGE,"E164"),sQuery(id+"F0.wireOp",EDGE,"E165"),sQuery(id+"F0.wireOp",EDGE,"E166"),sQuery(id+"F0.wireOp",EDGE,"E167"),sQuery(id+"F0.wireOp",EDGE,"E168"),sQuery(id+"F0.wireOp",EDGE,"E169"),sQuery(id+"F0.wireOp",EDGE,"E170"),sQuery(id+"F0.wireOp",EDGE,"E171"),sQuery(id+"F0.wireOp",EDGE,"E172"),sQuery(id+"F0.wireOp",EDGE,"E173"),sQuery(id+"F0.wireOp",EDGE,"E174"),sQuery(id+"F0.wireOp",EDGE,"E175"),sQuery(id+"F0.wireOp",EDGE,"E176"),sQuery(id+"F0.wireOp",EDGE,"E177"),sQuery(id+"F0.wireOp",EDGE,"E178"),sQuery(id+"F0.wireOp",EDGE,"E179"),sQuery(id+"F0.wireOp",EDGE,"E180"),sQuery(id+"F0.wireOp",EDGE,"E181"),sQuery(id+"F0.wireOp",EDGE,"E182"),sQuery(id+"F0.wireOp",EDGE,"E183"),sQuery(id+"F0.wireOp",EDGE,"E184"),sQuery(id+"F0.wireOp",EDGE,"E185"),sQuery(id+"F0.wireOp",EDGE,"E186"),sQuery(id+"F0.wireOp",EDGE,"E187"),sQuery(id+"F0.wireOp",EDGE,"E188"),sQuery(id+"F0.wireOp",EDGE,"E189"),sQuery(id+"F0.wireOp",EDGE,"E190"),sQuery(id+"F0.wireOp",EDGE,"E191"),sQuery(id+"F0.wireOp",EDGE,"E192"),sQuery(id+"F0.wireOp",EDGE,"E193"),sQuery(id+"F0.wireOp",EDGE,"E194"),sQuery(id+"F0.wireOp",EDGE,"E195"),sQuery(id+"F0.wireOp",EDGE,"E196"),sQuery(id+"F0.wireOp",EDGE,"E197"),sQuery(id+"F0.wireOp",EDGE,"E198"),sQuery(id+"F0.wireOp",EDGE,"E199"),sQuery(id+"F0.wireOp",EDGE,"E200"),sQuery(id+"F0.wireOp",EDGE,"E201"),sQuery(id+"F0.wireOp",EDGE,"E202"),sQuery(id+"F0.wireOp",EDGE,"E203"),sQuery(id+"F0.wireOp",EDGE,"E204"),sQuery(id+"F0.wireOp",EDGE,"E205"),sQuery(id+"F0.wireOp",EDGE,"E206"),sQuery(id+"F0.wireOp",EDGE,"E207"),sQuery(id+"F0.wireOp",EDGE,"E208"),sQuery(id+"F0.wireOp",EDGE,"E209"),sQuery(id+"F0.wireOp",EDGE,"E210"),sQuery(id+"F0.wireOp",EDGE,"E211"),sQuery(id+"F0.wireOp",EDGE,"E212"),sQuery(id+"F0.wireOp",EDGE,"E213"),sQuery(id+"F0.wireOp",EDGE,"E214"),sQuery(id+"F0.wireOp",EDGE,"E215"),sQuery(id+"F0.wireOp",EDGE,"E216"),sQuery(id+"F0.wireOp",EDGE,"E217"),sQuery(id+"F0.wireOp",EDGE,"E218"),sQuery(id+"F0.wireOp",EDGE,"E219"),sQuery(id+"F0.wireOp",EDGE,"E220"),sQuery(id+"F0.wireOp",EDGE,"E221"),sQuery(id+"F0.wireOp",EDGE,"E222"),sQuery(id+"F0.wireOp",EDGE,"E223"),sQuery(id+"F0.wireOp",EDGE,"E224"),sQuery(id+"F0.wireOp",EDGE,"E225"),sQuery(id+"F0.wireOp",EDGE,"E226"),sQuery(id+"F0.wireOp",EDGE,"E227"),sQuery(id+"F0.wireOp",EDGE,"E228"),sQuery(id+"F0.wireOp",EDGE,"E229"),sQuery(id+"F0.wireOp",EDGE,"E230"),sQuery(id+"F0.wireOp",EDGE,"E231"),sQuery(id+"F0.wireOp",EDGE,"E232"),sQuery(id+"F0.wireOp",EDGE,"E233"),sQuery(id+"F0.wireOp",EDGE,"E234"),sQuery(id+"F0.wireOp",EDGE,"E235"),sQuery(id+"F0.wireOp",EDGE,"E236"),sQuery(id+"F0.wireOp",EDGE,"E237"),sQuery(id+"F0.wireOp",EDGE,"E238"),sQuery(id+"F0.wireOp",EDGE,"E239"),sQuery(id+"F0.wireOp",EDGE,"E240"),sQuery(id+"F0.wireOp",EDGE,"E241"),sQuery(id+"F0.wireOp",EDGE,"E242"),sQuery(id+"F0.wireOp",EDGE,"E243"),sQuery(id+"F0.wireOp",EDGE,"E244"),sQuery(id+"F0.wireOp",EDGE,"E245"),sQuery(id+"F0.wireOp",EDGE,"E246"),sQuery(id+"F0.wireOp",EDGE,"E247"),sQuery(id+"F0.wireOp",EDGE,"E248"),sQuery(id+"F0.wireOp",EDGE,"E249"),sQuery(id+"F0.wireOp",EDGE,"E250"),sQuery(id+"F0.wireOp",EDGE,"E251"),sQuery(id+"F0.wireOp",EDGE,"E252"),sQuery(id+"F0.wireOp",EDGE,"E253"),sQuery(id+"F0.wireOp",EDGE,"E254"),sQuery(id+"F0.wireOp",EDGE,"E255"),sQuery(id+"F0.wireOp",EDGE,"E256"),sQuery(id+"F0.wireOp",EDGE,"E257"),sQuery(id+"F0.wireOp",EDGE,"E258"),sQuery(id+"F0.wireOp",EDGE,"E259"),sQuery(id+"F0.wireOp",EDGE,"E260"),sQuery(id+"F0.wireOp",EDGE,"E261"),sQuery(id+"F0.wireOp",EDGE,"E262"),sQuery(id+"F0.wireOp",EDGE,"E263"),sQuery(id+"F0.wireOp",EDGE,"E264"),sQuery(id+"F0.wireOp",EDGE,"E265"),sQuery(id+"F0.wireOp",EDGE,"E266"),sQuery(id+"F0.wireOp",EDGE,"E267"),sQuery(id+"F0.wireOp",EDGE,"E268"),sQuery(id+"F0.wireOp",EDGE,"E269"),sQuery(id+"F0.wireOp",EDGE,"E270"),sQuery(id+"F0.wireOp",EDGE,"E271"),sQuery(id+"F0.wireOp",EDGE,"E272"),sQuery(id+"F0.wireOp",EDGE,"E273"),sQuery(id+"F0.wireOp",EDGE,"E274"),sQuery(id+"F0.wireOp",EDGE,"E275"),sQuery(id+"F0.wireOp",EDGE,"E276"),sQuery(id+"F0.wireOp",EDGE,"E277"),sQuery(id+"F0.wireOp",EDGE,"E278"),sQuery(id+"F0.wireOp",EDGE,"E279"),sQuery(id+"F0.wireOp",EDGE,"E280"),sQuery(id+"F0.wireOp",EDGE,"E281"),sQuery(id+"F0.wireOp",EDGE,"E282"),sQuery(id+"F0.wireOp",EDGE,"E283"),sQuery(id+"F0.wireOp",EDGE,"E284"),sQuery(id+"F0.wireOp",EDGE,"E285"),sQuery(id+"F0.wireOp",EDGE,"E286"),sQuery(id+"F0.wireOp",EDGE,"E287"),sQuery(id+"F0.wireOp",EDGE,"E288"),sQuery(id+"F0.wireOp",EDGE,"E289"),sQuery(id+"F0.wireOp",EDGE,"E290"),sQuery(id+"F0.wireOp",EDGE,"E291"),sQuery(id+"F0.wireOp",EDGE,"E292"),sQuery(id+"F0.wireOp",EDGE,"E293"),sQuery(id+"F0.wireOp",EDGE,"E294"),sQuery(id+"F0.wireOp",EDGE,"E295"),sQuery(id+"F0.wireOp",EDGE,"E296"),sQuery(id+"F0.wireOp",EDGE,"E297"),sQuery(id+"F0.wireOp",EDGE,"E298"),sQuery(id+"F0.wireOp",EDGE,"E299"),sQuery(id+"F0.wireOp",EDGE,"E300"),sQuery(id+"F0.wireOp",EDGE,"E301"),sQuery(id+"F0.wireOp",EDGE,"E302"),sQuery(id+"F0.wireOp",EDGE,"E303"),sQuery(id+"F0.wireOp",EDGE,"E304"),sQuery(id+"F0.wireOp",EDGE,"E305"),sQuery(id+"F0.wireOp",EDGE,"E306"),sQuery(id+"F0.wireOp",EDGE,"E307"),sQuery(id+"F0.wireOp",EDGE,"E308"),sQuery(id+"F0.wireOp",EDGE,"E309"),sQuery(id+"F0.wireOp",EDGE,"E310"),sQuery(id+"F0.wireOp",EDGE,"E311"),sQuery(id+"F0.wireOp",EDGE,"E312"),sQuery(id+"F0.wireOp",EDGE,"E313"),sQuery(id+"F0.wireOp",EDGE,"E314"),sQuery(id+"F0.wireOp",EDGE,"E315"),sQuery(id+"F0.wireOp",EDGE,"E316"),sQuery(id+"F0.wireOp",EDGE,"E317"),sQuery(id+"F0.wireOp",EDGE,"E318"),sQuery(id+"F0.wireOp",EDGE,"E319"),sQuery(id+"F0.wireOp",EDGE,"E320"),sQuery(id+"F0.wireOp",EDGE,"E321"),sQuery(id+"F0.wireOp",EDGE,"E322"),sQuery(id+"F0.wireOp",EDGE,"E323"),sQuery(id+"F0.wireOp",EDGE,"E324"),sQuery(id+"F0.wireOp",EDGE,"E325"),sQuery(id+"F0.wireOp",EDGE,"E326"),sQuery(id+"F0.wireOp",EDGE,"E327"),sQuery(id+"F0.wireOp",EDGE,"E328"),sQuery(id+"F0.wireOp",EDGE,"E329"),sQuery(id+"F0.wireOp",EDGE,"E330"),sQuery(id+"F0.wireOp",EDGE,"E331"),sQuery(id+"F0.wireOp",EDGE,"E332"),sQuery(id+"F0.wireOp",EDGE,"E333"),sQuery(id+"F0.wireOp",EDGE,"E334"),sQuery(id+"F0.wireOp",EDGE,"E335"),sQuery(id+"F0.wireOp",EDGE,"E336"),sQuery(id+"F0.wireOp",EDGE,"E337"),sQuery(id+"F0.wireOp",EDGE,"E338"),sQuery(id+"F0.wireOp",EDGE,"E339"),sQuery(id+"F0.wireOp",EDGE,"E340"),sQuery(id+"F0.wireOp",EDGE,"E341"),sQuery(id+"F0.wireOp",EDGE,"E342"),sQuery(id+"F0.wireOp",EDGE,"E343"),sQuery(id+"F0.wireOp",EDGE,"E344"),sQuery(id+"F0.wireOp",EDGE,"E345"),sQuery(id+"F0.wireOp",EDGE,"E346"),sQuery(id+"F0.wireOp",EDGE,"E347"),sQuery(id+"F0.wireOp",EDGE,"E348"),sQuery(id+"F0.wireOp",EDGE,"E349"),sQuery(id+"F0.wireOp",EDGE,"E350"),sQuery(id+"F0.wireOp",EDGE,"E351"),sQuery(id+"F0.wireOp",EDGE,"E352"),sQuery(id+"F0.wireOp",EDGE,"E353"),sQuery(id+"F0.wireOp",EDGE,"E354"),sQuery(id+"F0.wireOp",EDGE,"E355"),sQuery(id+"F0.wireOp",EDGE,"E356"),sQuery(id+"F0.wireOp",EDGE,"E357"),sQuery(id+"F0.wireOp",EDGE,"E358"),sQuery(id+"F0.wireOp",EDGE,"E359"),sQuery(id+"F0.wireOp",EDGE,"E360"),sQuery(id+"F0.wireOp",EDGE,"E361"),sQuery(id+"F0.wireOp",EDGE,"E362"),sQuery(id+"F0.wireOp",EDGE,"E363"),sQuery(id+"F0.wireOp",EDGE,"E364"),sQuery(id+"F0.wireOp",EDGE,"E365"),sQuery(id+"F0.wireOp",EDGE,"E366"),sQuery(id+"F0.wireOp",EDGE,"E367"),sQuery(id+"F0.wireOp",EDGE,"E368"),sQuery(id+"F0.wireOp",EDGE,"E369"),sQuery(id+"F0.wireOp",EDGE,"E370"),sQuery(id+"F0.wireOp",EDGE,"E371"),sQuery(id+"F0.wireOp",EDGE,"E372"),sQuery(id+"F0.wireOp",EDGE,"E373"),sQuery(id+"F0.wireOp",EDGE,"E374"),sQuery(id+"F0.wireOp",EDGE,"E375"),sQuery(id+"F0.wireOp",EDGE,"E376"),sQuery(id+"F0.wireOp",EDGE,"E377"),sQuery(id+"F0.wireOp",EDGE,"E378"),sQuery(id+"F0.wireOp",EDGE,"E379"),sQuery(id+"F0.wireOp",EDGE,"E380"),sQuery(id+"F0.wireOp",EDGE,"E381"),sQuery(id+"F0.wireOp",EDGE,"E382"),sQuery(id+"F0.wireOp",EDGE,"E383"),sQuery(id+"F0.wireOp",EDGE,"E384"),sQuery(id+"F0.wireOp",EDGE,"E385"),sQuery(id+"F0.wireOp",EDGE,"E386"),sQuery(id+"F0.wireOp",EDGE,"E387"),sQuery(id+"F0.wireOp",EDGE,"E388"),sQuery(id+"F0.wireOp",EDGE,"E389")])],"isStart":false});
            var sketch = newSketch(context, id + "F2", { "sketchPlane" : qUnion([Q0])});
            skCircle(sketch, "E390", {"center": v(-10, 10) * mm, "radius": 1.52 * mm});
            skCircle(sketch, "E391", {"center": v(-10, -10) * mm, "radius": 1.52 * mm});
            skCircle(sketch, "E392", {"center": v(-104.5, 104.5) * mm, "radius": 1.65 * mm});
            skCircle(sketch, "E393", {"center": v(-104.5, -104.5) * mm, "radius": 1.65 * mm});
            skCircle(sketch, "E394", {"center": v(-44.45, 20.8) * mm, "radius": 3.56 * mm});
            skCircle(sketch, "E395", {"center": v(-44.45, -20.8) * mm, "radius": 2.55 * mm});
            skSolve(sketch);
        }
        {
            var Q0;
            Q0=qSketchRegion(id+"F2",true);
            extrude(context, id + "F3", {"entities" : qUnion([Q0]), "operationType" : NewBodyOperationType.REMOVE, "endBound" : BoundingType.THROUGH_ALL, "oppositeDirection" : true, "depth" : 25 * mm, "offsetDistance" : 25 * mm});
        }
        {
            var Q0;
            Q0=qCreatedBy(makeId("Top.planeOp"),FACE);
            var sketch = newSketch(context, id + "F4", { "sketchPlane" : qUnion([Q0])});
            skCircle(sketch, "E396", {"center": v(-44.45, 20.8) * mm, "radius": 1 * mm});
            skCircle(sketch, "E397", {"center": v(44.45, 20.8) * mm, "radius": 1 * mm});
            skCircle(sketch, "E398", {"center": v(-44.45, -20.8) * mm, "radius": 1 * mm});
            skCircle(sketch, "E399", {"center": v(44.45, -20.8) * mm, "radius": 1 * mm});
            skSolve(sketch);
        }
        {
            var Q0;
            Q0 = qSketchRegion(id + "F4", true);
            extrude(context, id + "F5", {"entities" : qUnion([Q0]), "oppositeDirection" : true, "depth" : 20 * mm, "offsetDistance" : 25 * mm});
        }
        {
            var Q0;
            Q0=makeQuery(id+"F1.opExtrude","CAP_FACE",FACE,{"disambiguationData":[OSD([sQuery(id+"F0.wireOp",EDGE,"E0"),sQuery(id+"F0.wireOp",EDGE,"E1"),sQuery(id+"F0.wireOp",EDGE,"E2"),sQuery(id+"F0.wireOp",EDGE,"E3"),sQuery(id+"F0.wireOp",EDGE,"E4"),sQuery(id+"F0.wireOp",EDGE,"E5"),sQuery(id+"F0.wireOp",EDGE,"E6"),sQuery(id+"F0.wireOp",EDGE,"E7"),sQuery(id+"F0.wireOp",EDGE,"E8"),sQuery(id+"F0.wireOp",EDGE,"E9"),sQuery(id+"F0.wireOp",EDGE,"E10"),sQuery(id+"F0.wireOp",EDGE,"E11"),sQuery(id+"F0.wireOp",EDGE,"E12"),sQuery(id+"F0.wireOp",EDGE,"E13"),sQuery(id+"F0.wireOp",EDGE,"E14"),sQuery(id+"F0.wireOp",EDGE,"E15"),sQuery(id+"F0.wireOp",EDGE,"E16"),sQuery(id+"F0.wireOp",EDGE,"E17"),sQuery(id+"F0.wireOp",EDGE,"E18"),sQuery(id+"F0.wireOp",EDGE,"E19"),sQuery(id+"F0.wireOp",EDGE,"E20"),sQuery(id+"F0.wireOp",EDGE,"E21"),sQuery(id+"F0.wireOp",EDGE,"E22"),sQuery(id+"F0.wireOp",EDGE,"E23"),sQuery(id+"F0.wireOp",EDGE,"E24"),sQuery(id+"F0.wireOp",EDGE,"E25"),sQuery(id+"F0.wireOp",EDGE,"E26"),sQuery(id+"F0.wireOp",EDGE,"E27"),sQuery(id+"F0.wireOp",EDGE,"E28"),sQuery(id+"F0.wireOp",EDGE,"E29"),sQuery(id+"F0.wireOp",EDGE,"E30"),sQuery(id+"F0.wireOp",EDGE,"E31"),sQuery(id+"F0.wireOp",EDGE,"E32"),sQuery(id+"F0.wireOp",EDGE,"E33"),sQuery(id+"F0.wireOp",EDGE,"E34"),sQuery(id+"F0.wireOp",EDGE,"E35"),sQuery(id+"F0.wireOp",EDGE,"E36"),sQuery(id+"F0.wireOp",EDGE,"E37"),sQuery(id+"F0.wireOp",EDGE,"E38"),sQuery(id+"F0.wireOp",EDGE,"E39"),sQuery(id+"F0.wireOp",EDGE,"E40"),sQuery(id+"F0.wireOp",EDGE,"E41"),sQuery(id+"F0.wireOp",EDGE,"E42"),sQuery(id+"F0.wireOp",EDGE,"E43"),sQuery(id+"F0.wireOp",EDGE,"E44"),sQuery(id+"F0.wireOp",EDGE,"E45"),sQuery(id+"F0.wireOp",EDGE,"E46"),sQuery(id+"F0.wireOp",EDGE,"E47"),sQuery(id+"F0.wireOp",EDGE,"E48"),sQuery(id+"F0.wireOp",EDGE,"E49"),sQuery(id+"F0.wireOp",EDGE,"E50"),sQuery(id+"F0.wireOp",EDGE,"E51"),sQuery(id+"F0.wireOp",EDGE,"E52"),sQuery(id+"F0.wireOp",EDGE,"E53"),sQuery(id+"F0.wireOp",EDGE,"E54"),sQuery(id+"F0.wireOp",EDGE,"E55"),sQuery(id+"F0.wireOp",EDGE,"E56"),sQuery(id+"F0.wireOp",EDGE,"E57"),sQuery(id+"F0.wireOp",EDGE,"E58"),sQuery(id+"F0.wireOp",EDGE,"E59"),sQuery(id+"F0.wireOp",EDGE,"E60"),sQuery(id+"F0.wireOp",EDGE,"E61"),sQuery(id+"F0.wireOp",EDGE,"E62"),sQuery(id+"F0.wireOp",EDGE,"E63"),sQuery(id+"F0.wireOp",EDGE,"E64"),sQuery(id+"F0.wireOp",EDGE,"E65"),sQuery(id+"F0.wireOp",EDGE,"E66"),sQuery(id+"F0.wireOp",EDGE,"E67"),sQuery(id+"F0.wireOp",EDGE,"E68"),sQuery(id+"F0.wireOp",EDGE,"E69"),sQuery(id+"F0.wireOp",EDGE,"E70"),sQuery(id+"F0.wireOp",EDGE,"E71"),sQuery(id+"F0.wireOp",EDGE,"E72"),sQuery(id+"F0.wireOp",EDGE,"E73"),sQuery(id+"F0.wireOp",EDGE,"E74"),sQuery(id+"F0.wireOp",EDGE,"E75"),sQuery(id+"F0.wireOp",EDGE,"E76"),sQuery(id+"F0.wireOp",EDGE,"E77"),sQuery(id+"F0.wireOp",EDGE,"E78"),sQuery(id+"F0.wireOp",EDGE,"E79"),sQuery(id+"F0.wireOp",EDGE,"E80"),sQuery(id+"F0.wireOp",EDGE,"E81"),sQuery(id+"F0.wireOp",EDGE,"E82"),sQuery(id+"F0.wireOp",EDGE,"E83"),sQuery(id+"F0.wireOp",EDGE,"E84"),sQuery(id+"F0.wireOp",EDGE,"E85"),sQuery(id+"F0.wireOp",EDGE,"E86"),sQuery(id+"F0.wireOp",EDGE,"E87"),sQuery(id+"F0.wireOp",EDGE,"E88"),sQuery(id+"F0.wireOp",EDGE,"E89"),sQuery(id+"F0.wireOp",EDGE,"E90"),sQuery(id+"F0.wireOp",EDGE,"E91"),sQuery(id+"F0.wireOp",EDGE,"E92"),sQuery(id+"F0.wireOp",EDGE,"E93"),sQuery(id+"F0.wireOp",EDGE,"E94"),sQuery(id+"F0.wireOp",EDGE,"E95"),sQuery(id+"F0.wireOp",EDGE,"E96"),sQuery(id+"F0.wireOp",EDGE,"E97"),sQuery(id+"F0.wireOp",EDGE,"E98"),sQuery(id+"F0.wireOp",EDGE,"E99"),sQuery(id+"F0.wireOp",EDGE,"E100"),sQuery(id+"F0.wireOp",EDGE,"E101"),sQuery(id+"F0.wireOp",EDGE,"E102"),sQuery(id+"F0.wireOp",EDGE,"E103"),sQuery(id+"F0.wireOp",EDGE,"E104"),sQuery(id+"F0.wireOp",EDGE,"E105"),sQuery(id+"F0.wireOp",EDGE,"E106"),sQuery(id+"F0.wireOp",EDGE,"E107"),sQuery(id+"F0.wireOp",EDGE,"E108"),sQuery(id+"F0.wireOp",EDGE,"E109"),sQuery(id+"F0.wireOp",EDGE,"E110"),sQuery(id+"F0.wireOp",EDGE,"E111"),sQuery(id+"F0.wireOp",EDGE,"E112"),sQuery(id+"F0.wireOp",EDGE,"E113"),sQuery(id+"F0.wireOp",EDGE,"E114"),sQuery(id+"F0.wireOp",EDGE,"E115"),sQuery(id+"F0.wireOp",EDGE,"E116"),sQuery(id+"F0.wireOp",EDGE,"E117"),sQuery(id+"F0.wireOp",EDGE,"E118"),sQuery(id+"F0.wireOp",EDGE,"E119"),sQuery(id+"F0.wireOp",EDGE,"E120"),sQuery(id+"F0.wireOp",EDGE,"E121"),sQuery(id+"F0.wireOp",EDGE,"E122"),sQuery(id+"F0.wireOp",EDGE,"E123"),sQuery(id+"F0.wireOp",EDGE,"E124"),sQuery(id+"F0.wireOp",EDGE,"E125"),sQuery(id+"F0.wireOp",EDGE,"E126"),sQuery(id+"F0.wireOp",EDGE,"E127"),sQuery(id+"F0.wireOp",EDGE,"E128"),sQuery(id+"F0.wireOp",EDGE,"E129"),sQuery(id+"F0.wireOp",EDGE,"E130"),sQuery(id+"F0.wireOp",EDGE,"E131"),sQuery(id+"F0.wireOp",EDGE,"E132"),sQuery(id+"F0.wireOp",EDGE,"E133"),sQuery(id+"F0.wireOp",EDGE,"E134"),sQuery(id+"F0.wireOp",EDGE,"E135"),sQuery(id+"F0.wireOp",EDGE,"E136"),sQuery(id+"F0.wireOp",EDGE,"E137"),sQuery(id+"F0.wireOp",EDGE,"E138"),sQuery(id+"F0.wireOp",EDGE,"E139"),sQuery(id+"F0.wireOp",EDGE,"E140"),sQuery(id+"F0.wireOp",EDGE,"E141"),sQuery(id+"F0.wireOp",EDGE,"E142"),sQuery(id+"F0.wireOp",EDGE,"E143"),sQuery(id+"F0.wireOp",EDGE,"E144"),sQuery(id+"F0.wireOp",EDGE,"E145"),sQuery(id+"F0.wireOp",EDGE,"E146"),sQuery(id+"F0.wireOp",EDGE,"E147"),sQuery(id+"F0.wireOp",EDGE,"E148"),sQuery(id+"F0.wireOp",EDGE,"E149"),sQuery(id+"F0.wireOp",EDGE,"E150"),sQuery(id+"F0.wireOp",EDGE,"E151"),sQuery(id+"F0.wireOp",EDGE,"E152"),sQuery(id+"F0.wireOp",EDGE,"E153"),sQuery(id+"F0.wireOp",EDGE,"E154"),sQuery(id+"F0.wireOp",EDGE,"E155"),sQuery(id+"F0.wireOp",EDGE,"E156"),sQuery(id+"F0.wireOp",EDGE,"E157"),sQuery(id+"F0.wireOp",EDGE,"E158"),sQuery(id+"F0.wireOp",EDGE,"E159"),sQuery(id+"F0.wireOp",EDGE,"E160"),sQuery(id+"F0.wireOp",EDGE,"E161"),sQuery(id+"F0.wireOp",EDGE,"E162"),sQuery(id+"F0.wireOp",EDGE,"E163"),sQuery(id+"F0.wireOp",EDGE,"E164"),sQuery(id+"F0.wireOp",EDGE,"E165"),sQuery(id+"F0.wireOp",EDGE,"E166"),sQuery(id+"F0.wireOp",EDGE,"E167"),sQuery(id+"F0.wireOp",EDGE,"E168"),sQuery(id+"F0.wireOp",EDGE,"E169"),sQuery(id+"F0.wireOp",EDGE,"E170"),sQuery(id+"F0.wireOp",EDGE,"E171"),sQuery(id+"F0.wireOp",EDGE,"E172"),sQuery(id+"F0.wireOp",EDGE,"E173"),sQuery(id+"F0.wireOp",EDGE,"E174"),sQuery(id+"F0.wireOp",EDGE,"E175"),sQuery(id+"F0.wireOp",EDGE,"E176"),sQuery(id+"F0.wireOp",EDGE,"E177"),sQuery(id+"F0.wireOp",EDGE,"E178"),sQuery(id+"F0.wireOp",EDGE,"E179"),sQuery(id+"F0.wireOp",EDGE,"E180"),sQuery(id+"F0.wireOp",EDGE,"E181"),sQuery(id+"F0.wireOp",EDGE,"E182"),sQuery(id+"F0.wireOp",EDGE,"E183"),sQuery(id+"F0.wireOp",EDGE,"E184"),sQuery(id+"F0.wireOp",EDGE,"E185"),sQuery(id+"F0.wireOp",EDGE,"E186"),sQuery(id+"F0.wireOp",EDGE,"E187"),sQuery(id+"F0.wireOp",EDGE,"E188"),sQuery(id+"F0.wireOp",EDGE,"E189"),sQuery(id+"F0.wireOp",EDGE,"E190"),sQuery(id+"F0.wireOp",EDGE,"E191"),sQuery(id+"F0.wireOp",EDGE,"E192"),sQuery(id+"F0.wireOp",EDGE,"E193"),sQuery(id+"F0.wireOp",EDGE,"E194"),sQuery(id+"F0.wireOp",EDGE,"E195"),sQuery(id+"F0.wireOp",EDGE,"E196"),sQuery(id+"F0.wireOp",EDGE,"E197"),sQuery(id+"F0.wireOp",EDGE,"E198"),sQuery(id+"F0.wireOp",EDGE,"E199"),sQuery(id+"F0.wireOp",EDGE,"E200"),sQuery(id+"F0.wireOp",EDGE,"E201"),sQuery(id+"F0.wireOp",EDGE,"E202"),sQuery(id+"F0.wireOp",EDGE,"E203"),sQuery(id+"F0.wireOp",EDGE,"E204"),sQuery(id+"F0.wireOp",EDGE,"E205"),sQuery(id+"F0.wireOp",EDGE,"E206"),sQuery(id+"F0.wireOp",EDGE,"E207"),sQuery(id+"F0.wireOp",EDGE,"E208"),sQuery(id+"F0.wireOp",EDGE,"E209"),sQuery(id+"F0.wireOp",EDGE,"E210"),sQuery(id+"F0.wireOp",EDGE,"E211"),sQuery(id+"F0.wireOp",EDGE,"E212"),sQuery(id+"F0.wireOp",EDGE,"E213"),sQuery(id+"F0.wireOp",EDGE,"E214"),sQuery(id+"F0.wireOp",EDGE,"E215"),sQuery(id+"F0.wireOp",EDGE,"E216"),sQuery(id+"F0.wireOp",EDGE,"E217"),sQuery(id+"F0.wireOp",EDGE,"E218"),sQuery(id+"F0.wireOp",EDGE,"E219"),sQuery(id+"F0.wireOp",EDGE,"E220"),sQuery(id+"F0.wireOp",EDGE,"E221"),sQuery(id+"F0.wireOp",EDGE,"E222"),sQuery(id+"F0.wireOp",EDGE,"E223"),sQuery(id+"F0.wireOp",EDGE,"E224"),sQuery(id+"F0.wireOp",EDGE,"E225"),sQuery(id+"F0.wireOp",EDGE,"E226"),sQuery(id+"F0.wireOp",EDGE,"E227"),sQuery(id+"F0.wireOp",EDGE,"E228"),sQuery(id+"F0.wireOp",EDGE,"E229"),sQuery(id+"F0.wireOp",EDGE,"E230"),sQuery(id+"F0.wireOp",EDGE,"E231"),sQuery(id+"F0.wireOp",EDGE,"E232"),sQuery(id+"F0.wireOp",EDGE,"E233"),sQuery(id+"F0.wireOp",EDGE,"E234"),sQuery(id+"F0.wireOp",EDGE,"E235"),sQuery(id+"F0.wireOp",EDGE,"E236"),sQuery(id+"F0.wireOp",EDGE,"E237"),sQuery(id+"F0.wireOp",EDGE,"E238"),sQuery(id+"F0.wireOp",EDGE,"E239"),sQuery(id+"F0.wireOp",EDGE,"E240"),sQuery(id+"F0.wireOp",EDGE,"E241"),sQuery(id+"F0.wireOp",EDGE,"E242"),sQuery(id+"F0.wireOp",EDGE,"E243"),sQuery(id+"F0.wireOp",EDGE,"E244"),sQuery(id+"F0.wireOp",EDGE,"E245"),sQuery(id+"F0.wireOp",EDGE,"E246"),sQuery(id+"F0.wireOp",EDGE,"E247"),sQuery(id+"F0.wireOp",EDGE,"E248"),sQuery(id+"F0.wireOp",EDGE,"E249"),sQuery(id+"F0.wireOp",EDGE,"E250"),sQuery(id+"F0.wireOp",EDGE,"E251"),sQuery(id+"F0.wireOp",EDGE,"E252"),sQuery(id+"F0.wireOp",EDGE,"E253"),sQuery(id+"F0.wireOp",EDGE,"E254"),sQuery(id+"F0.wireOp",EDGE,"E255"),sQuery(id+"F0.wireOp",EDGE,"E256"),sQuery(id+"F0.wireOp",EDGE,"E257"),sQuery(id+"F0.wireOp",EDGE,"E258"),sQuery(id+"F0.wireOp",EDGE,"E259"),sQuery(id+"F0.wireOp",EDGE,"E260"),sQuery(id+"F0.wireOp",EDGE,"E261"),sQuery(id+"F0.wireOp",EDGE,"E262"),sQuery(id+"F0.wireOp",EDGE,"E263"),sQuery(id+"F0.wireOp",EDGE,"E264"),sQuery(id+"F0.wireOp",EDGE,"E265"),sQuery(id+"F0.wireOp",EDGE,"E266"),sQuery(id+"F0.wireOp",EDGE,"E267"),sQuery(id+"F0.wireOp",EDGE,"E268"),sQuery(id+"F0.wireOp",EDGE,"E269"),sQuery(id+"F0.wireOp",EDGE,"E270"),sQuery(id+"F0.wireOp",EDGE,"E271"),sQuery(id+"F0.wireOp",EDGE,"E272"),sQuery(id+"F0.wireOp",EDGE,"E273"),sQuery(id+"F0.wireOp",EDGE,"E274"),sQuery(id+"F0.wireOp",EDGE,"E275"),sQuery(id+"F0.wireOp",EDGE,"E276"),sQuery(id+"F0.wireOp",EDGE,"E277"),sQuery(id+"F0.wireOp",EDGE,"E278"),sQuery(id+"F0.wireOp",EDGE,"E279"),sQuery(id+"F0.wireOp",EDGE,"E280"),sQuery(id+"F0.wireOp",EDGE,"E281"),sQuery(id+"F0.wireOp",EDGE,"E282"),sQuery(id+"F0.wireOp",EDGE,"E283"),sQuery(id+"F0.wireOp",EDGE,"E284"),sQuery(id+"F0.wireOp",EDGE,"E285"),sQuery(id+"F0.wireOp",EDGE,"E286"),sQuery(id+"F0.wireOp",EDGE,"E287"),sQuery(id+"F0.wireOp",EDGE,"E288"),sQuery(id+"F0.wireOp",EDGE,"E289"),sQuery(id+"F0.wireOp",EDGE,"E290"),sQuery(id+"F0.wireOp",EDGE,"E291"),sQuery(id+"F0.wireOp",EDGE,"E292"),sQuery(id+"F0.wireOp",EDGE,"E293"),sQuery(id+"F0.wireOp",EDGE,"E294"),sQuery(id+"F0.wireOp",EDGE,"E295"),sQuery(id+"F0.wireOp",EDGE,"E296"),sQuery(id+"F0.wireOp",EDGE,"E297"),sQuery(id+"F0.wireOp",EDGE,"E298"),sQuery(id+"F0.wireOp",EDGE,"E299"),sQuery(id+"F0.wireOp",EDGE,"E300"),sQuery(id+"F0.wireOp",EDGE,"E301"),sQuery(id+"F0.wireOp",EDGE,"E302"),sQuery(id+"F0.wireOp",EDGE,"E303"),sQuery(id+"F0.wireOp",EDGE,"E304"),sQuery(id+"F0.wireOp",EDGE,"E305"),sQuery(id+"F0.wireOp",EDGE,"E306"),sQuery(id+"F0.wireOp",EDGE,"E307"),sQuery(id+"F0.wireOp",EDGE,"E308"),sQuery(id+"F0.wireOp",EDGE,"E309"),sQuery(id+"F0.wireOp",EDGE,"E310"),sQuery(id+"F0.wireOp",EDGE,"E311"),sQuery(id+"F0.wireOp",EDGE,"E312"),sQuery(id+"F0.wireOp",EDGE,"E313"),sQuery(id+"F0.wireOp",EDGE,"E314"),sQuery(id+"F0.wireOp",EDGE,"E315"),sQuery(id+"F0.wireOp",EDGE,"E316"),sQuery(id+"F0.wireOp",EDGE,"E317"),sQuery(id+"F0.wireOp",EDGE,"E318"),sQuery(id+"F0.wireOp",EDGE,"E319"),sQuery(id+"F0.wireOp",EDGE,"E320"),sQuery(id+"F0.wireOp",EDGE,"E321"),sQuery(id+"F0.wireOp",EDGE,"E322"),sQuery(id+"F0.wireOp",EDGE,"E323"),sQuery(id+"F0.wireOp",EDGE,"E324"),sQuery(id+"F0.wireOp",EDGE,"E325"),sQuery(id+"F0.wireOp",EDGE,"E326"),sQuery(id+"F0.wireOp",EDGE,"E327"),sQuery(id+"F0.wireOp",EDGE,"E328"),sQuery(id+"F0.wireOp",EDGE,"E329"),sQuery(id+"F0.wireOp",EDGE,"E330"),sQuery(id+"F0.wireOp",EDGE,"E331"),sQuery(id+"F0.wireOp",EDGE,"E332"),sQuery(id+"F0.wireOp",EDGE,"E333"),sQuery(id+"F0.wireOp",EDGE,"E334"),sQuery(id+"F0.wireOp",EDGE,"E335"),sQuery(id+"F0.wireOp",EDGE,"E336"),sQuery(id+"F0.wireOp",EDGE,"E337"),sQuery(id+"F0.wireOp",EDGE,"E338"),sQuery(id+"F0.wireOp",EDGE,"E339"),sQuery(id+"F0.wireOp",EDGE,"E340"),sQuery(id+"F0.wireOp",EDGE,"E341"),sQuery(id+"F0.wireOp",EDGE,"E342"),sQuery(id+"F0.wireOp",EDGE,"E343"),sQuery(id+"F0.wireOp",EDGE,"E344"),sQuery(id+"F0.wireOp",EDGE,"E345"),sQuery(id+"F0.wireOp",EDGE,"E346"),sQuery(id+"F0.wireOp",EDGE,"E347"),sQuery(id+"F0.wireOp",EDGE,"E348"),sQuery(id+"F0.wireOp",EDGE,"E349"),sQuery(id+"F0.wireOp",EDGE,"E350"),sQuery(id+"F0.wireOp",EDGE,"E351"),sQuery(id+"F0.wireOp",EDGE,"E352"),sQuery(id+"F0.wireOp",EDGE,"E353"),sQuery(id+"F0.wireOp",EDGE,"E354"),sQuery(id+"F0.wireOp",EDGE,"E355"),sQuery(id+"F0.wireOp",EDGE,"E356"),sQuery(id+"F0.wireOp",EDGE,"E357"),sQuery(id+"F0.wireOp",EDGE,"E358"),sQuery(id+"F0.wireOp",EDGE,"E359"),sQuery(id+"F0.wireOp",EDGE,"E360"),sQuery(id+"F0.wireOp",EDGE,"E361"),sQuery(id+"F0.wireOp",EDGE,"E362"),sQuery(id+"F0.wireOp",EDGE,"E363"),sQuery(id+"F0.wireOp",EDGE,"E364"),sQuery(id+"F0.wireOp",EDGE,"E365"),sQuery(id+"F0.wireOp",EDGE,"E366"),sQuery(id+"F0.wireOp",EDGE,"E367"),sQuery(id+"F0.wireOp",EDGE,"E368"),sQuery(id+"F0.wireOp",EDGE,"E369"),sQuery(id+"F0.wireOp",EDGE,"E370"),sQuery(id+"F0.wireOp",EDGE,"E371"),sQuery(id+"F0.wireOp",EDGE,"E372"),sQuery(id+"F0.wireOp",EDGE,"E373"),sQuery(id+"F0.wireOp",EDGE,"E374"),sQuery(id+"F0.wireOp",EDGE,"E375"),sQuery(id+"F0.wireOp",EDGE,"E376"),sQuery(id+"F0.wireOp",EDGE,"E377"),sQuery(id+"F0.wireOp",EDGE,"E378"),sQuery(id+"F0.wireOp",EDGE,"E379"),sQuery(id+"F0.wireOp",EDGE,"E380"),sQuery(id+"F0.wireOp",EDGE,"E381"),sQuery(id+"F0.wireOp",EDGE,"E382"),sQuery(id+"F0.wireOp",EDGE,"E383"),sQuery(id+"F0.wireOp",EDGE,"E384"),sQuery(id+"F0.wireOp",EDGE,"E385"),sQuery(id+"F0.wireOp",EDGE,"E386"),sQuery(id+"F0.wireOp",EDGE,"E387"),sQuery(id+"F0.wireOp",EDGE,"E388"),sQuery(id+"F0.wireOp",EDGE,"E389")])],"isStart":false});
            var sketch = newSketch(context, id + "F6", { "sketchPlane" : qUnion([Q0])});
            skCircle(sketch, "E400.0", {"center": v(-44.45, 20.8) * mm, "radius": 3.56 * mm});
            skCircle(sketch, "E401.0", {"center": v(-44.45, -20.8) * mm, "radius": 2.55 * mm});
            skCircle(sketch, "E402.0", {"center": v(44.45, 20.8) * mm, "radius": 3.56 * mm});
            skCircle(sketch, "E403.0", {"center": v(44.45, -20.8) * mm, "radius": 2.55 * mm});
            skSolve(sketch);
        }
        {
            var Q0;
            Q0 = qSketchRegion(id + "F6", true);
            extrude(context, id + "F7", {"entities" : qUnion([Q0]), "operationType" : NewBodyOperationType.ADD, "oppositeDirection" : true, "depth" : 4.75 * mm, "offsetDistance" : 25 * mm});
        }
    });
